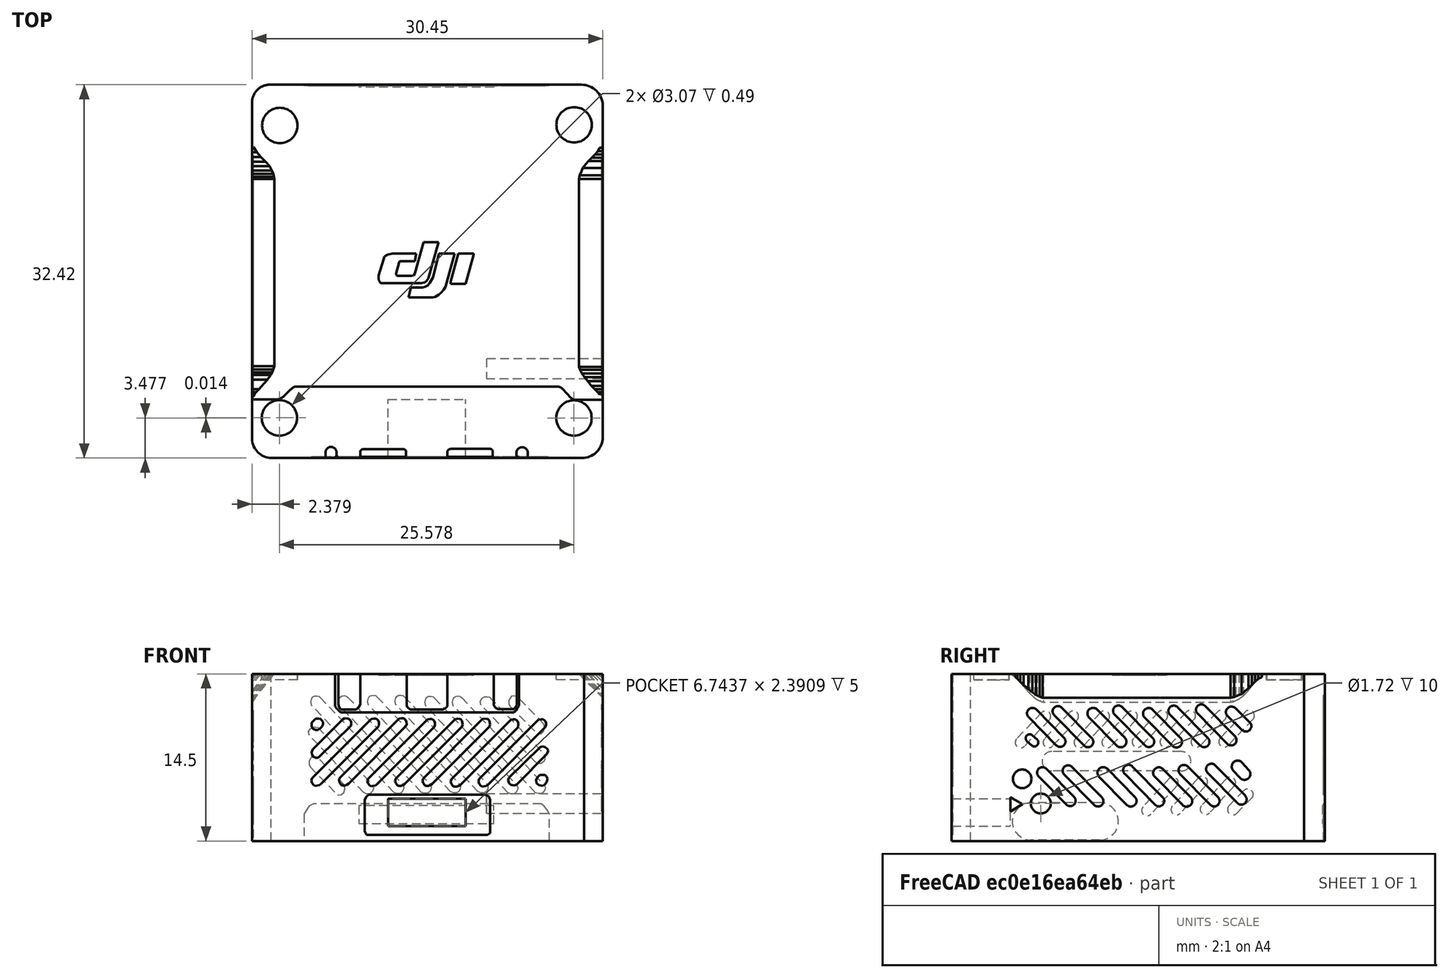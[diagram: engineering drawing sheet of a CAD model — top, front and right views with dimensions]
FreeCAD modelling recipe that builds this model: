
FCSTD DOCUMENT  (FreeCAD 0.19R24267 +99 (Git))
Label: O3
License: All rights reserved
LicenseURL: http://en.wikipedia.org/wiki/All_rights_reserved
objects: Sketcher::SketchObject×13, PartDesign::Pocket×10, Image::ImagePlane×5, PartDesign::Pad×1, PartDesign::Groove×1, PartDesign::SubtractivePipe×1, PartDesign::Body×1, Mesh::Feature×1
note: 40 computed .brp shape members not serialized (recipe doc carries the construction recipe); baked Part::Feature solids carry a one-line shape summary decoded from their .brp

FEATURE [Image::ImagePlane] ImagePlane
  XSize = 48.9538
  YSize = 52.2174
FEATURE [Sketcher::SketchObject] Sketch
  FullyConstrained = false
  MapMode = 5
  Support = -> [XY_Plane]
  sketch-geometry (8):
    g0: LineSegment StartX=-16.2841 StartY=17.4805 StartZ=0 EndX=10.6683 EndY=17.4805 EndZ=0
    g1: ArcOfCircle CenterX=10.6683 CenterY=15.6352 CenterZ=0 NormalX=0 NormalY=0 NormalZ=1 AngleXU=0 Radius=1.84529 StartAngle=0.0193587 EndAngle=1.5708
    g2: LineSegment StartX=12.5133 StartY=15.6709 StartZ=0 EndX=12.5133 EndY=-13.1285 EndZ=0
    g3: ArcOfCircle CenterX=10.6918 CenterY=-13.1285 CenterZ=0 NormalX=0 NormalY=0 NormalZ=1 AngleXU=0 Radius=1.82149 StartAngle=4.82467 EndAngle=6.28319
    g4: LineSegment StartX=10.8959 StartY=-14.9386 StartZ=0 EndX=-16.2285 EndY=-14.9386 EndZ=0
    g5: ArcOfCircle CenterX=-16.2285 CenterY=-13.2275 CenterZ=0 NormalX=0 NormalY=0 NormalZ=1 AngleXU=0 Radius=1.71109 StartAngle=3.16988 EndAngle=4.71239
    g6: LineSegment StartX=-17.9389 StartY=-13.2759 StartZ=0 EndX=-17.9389 EndY=15.9202 EndZ=0
    g7: ArcOfCircle CenterX=-16.3759 CenterY=15.9202 CenterZ=0 NormalX=0 NormalY=0 NormalZ=1 AngleXU=0 Radius=1.56302 StartAngle=1.51209 EndAngle=3.14159
  constraints (12):
    c: Horizontal(g0)
    c: Tangent(g0,g1) = 1.5708
    c: Coincident(g1,g2)
    c: Vertical(g2)
    c: Tangent(g2,g3) = 1.5708
    c: Coincident(g3,g4)
    c: Horizontal(g4)
    c: Tangent(g4,g5) = 1.5708
    c: Coincident(g5,g6)
    c: Vertical(g6)
    c: Tangent(g6,g7) = 1.5708
    c: Coincident(g7,g0)
FEATURE [PartDesign::Pad] Pad
  Direction = (1,1,1)
  Length = 14.5
  Length2 = 100
  Profile = -> Sketch
  Type = 0
FEATURE [Sketcher::SketchObject] Sketch001
  FullyConstrained = false
  MapMode = 5
  Placement = pos=(0,0,14.5) rot=(0,0,1;0rad)
  Support = -> [Pad]
  sketch-geometry (4):
    g0: Circle CenterX=-15.5269 CenterY=13.9364 CenterZ=0 NormalX=0 NormalY=0 NormalZ=1 AngleXU=0 Radius=1.53652
    g1: Circle CenterX=10.0286 CenterY=13.9974 CenterZ=0 NormalX=0 NormalY=0 NormalZ=1 AngleXU=0 Radius=1.53652
    g2: Circle CenterX=-15.561 CenterY=-11.4486 CenterZ=0 NormalX=0 NormalY=0 NormalZ=1 AngleXU=0 Radius=1.53652
    g3: Circle CenterX=10.0174 CenterY=-11.4626 CenterZ=0 NormalX=0 NormalY=0 NormalZ=1 AngleXU=0 Radius=1.53652
FEATURE [PartDesign::Pocket] Pocket
  BaseFeature = -> Pad
  Length = 0.5
  Length2 = 100
  Profile = -> Sketch001
  Type = 0
FEATURE [Sketcher::SketchObject] Sketch002
  FullyConstrained = false
  MapMode = 5
  Placement = pos=(0,0,14.5) rot=(0,0,1;0rad)
  Support = -> [Pocket]
  sketch-geometry (49):
    g0: LineSegment StartX=-3.66775 StartY=2.80694 StartZ=0 EndX=-5.73284 EndY=2.80694 EndZ=0
    g1: LineSegment StartX=-5.73284 StartY=2.80694 StartZ=0 EndX=-6.1577 EndY=2.70892 EndZ=0
    g2: LineSegment StartX=-6.1577 StartY=2.70892 StartZ=0 EndX=-6.42677 EndY=2.55314 EndZ=0
    g3: LineSegment StartX=-6.42677 StartY=2.55314 StartZ=0 EndX=-6.5157 EndY=2.35716 EndZ=0
    g4: LineSegment StartX=-6.5157 StartY=2.35716 StartZ=0 EndX=-6.9475 EndY=0.92689 EndZ=0
    g5: LineSegment StartX=-6.9475 StartY=0.92689 StartZ=0 EndX=-6.957 EndY=0.670578 EndZ=0
    g6: LineSegment StartX=-6.957 StartY=0.670578 StartZ=0 EndX=-6.92852 EndY=0.480717 EndZ=0
    g7: LineSegment StartX=-6.92852 StartY=0.480717 StartZ=0 EndX=-6.85411 EndY=0.359586 EndZ=0
    g8: LineSegment StartX=-6.85411 StartY=0.359586 StartZ=0 EndX=-6.79407 EndY=0.288105 EndZ=0
    g9: LineSegment StartX=-6.79407 StartY=0.288105 StartZ=0 EndX=-6.74546 EndY=0.256653 EndZ=0
    g10: LineSegment StartX=-6.74546 StartY=0.256653 StartZ=0 EndX=-3.2332 EndY=0.256653 EndZ=0
    g11: LineSegment StartX=-3.2332 StartY=0.256653 StartZ=0 EndX=-2.93381 EndY=0.321952 EndZ=0
    g12: LineSegment StartX=-2.93381 StartY=0.321952 StartZ=0 EndX=-2.79803 EndY=0.434318 EndZ=0
    g13: LineSegment StartX=-2.79803 StartY=0.434318 StartZ=0 EndX=-2.63651 EndY=0.663731 EndZ=0
    g14: LineSegment StartX=-2.63651 StartY=0.663731 StartZ=0 EndX=-1.72995 EndY=3.79902 EndZ=0
    g15: LineSegment StartX=-1.72995 StartY=3.79902 StartZ=0 EndX=-3.0436 EndY=3.79902 EndZ=0
    g16: LineSegment StartX=-3.0436 StartY=3.79902 StartZ=0 EndX=-3.79676 EndY=1.0627 EndZ=0
    g17: LineSegment StartX=-3.79676 StartY=1.0627 StartZ=0 EndX=-3.91067 EndY=0.929798 EndZ=0
    g18: LineSegment StartX=-3.91067 StartY=0.929798 StartZ=0 EndX=-4.08155 EndY=0.882333 EndZ=0
    g19: LineSegment StartX=-4.08155 StartY=0.882333 StartZ=0 EndX=-5.34413 EndY=0.882333 EndZ=0
    g20: LineSegment StartX=-5.34413 StartY=0.882333 StartZ=0 EndX=-5.42956 EndY=0.96777 EndZ=0
    g21: LineSegment StartX=-5.42956 StartY=0.96777 StartZ=0 EndX=-5.42956 EndY=1.11966 EndZ=0
    g22: LineSegment StartX=-5.42956 StartY=1.11966 StartZ=0 EndX=-5.18132 EndY=2.01186 EndZ=0
    g23: LineSegment StartX=-5.18132 StartY=2.01186 StartZ=0 EndX=-5.14987 EndY=2.11479 EndZ=0
    g24: LineSegment StartX=-5.14987 StartY=2.11479 StartZ=0 EndX=-5.10984 EndY=2.16054 EndZ=0
    g25: LineSegment StartX=-5.10984 StartY=2.16054 StartZ=0 EndX=-3.79458 EndY=2.16054 EndZ=0
    g26: LineSegment StartX=-3.79458 StartY=2.16054 StartZ=0 EndX=-3.66775 EndY=2.80694 EndZ=0
    g27: LineSegment StartX=-1.69511 StartY=2.81981 StartZ=0 EndX=-0.339263 EndY=2.81981 EndZ=0
    g28: LineSegment StartX=-0.339263 StartY=2.81981 StartZ=0 EndX=-1.14003 EndY=-0.062406 EndZ=0
    g29: LineSegment StartX=-1.14003 StartY=-0.062406 StartZ=0 EndX=-1.30548 EndY=-0.316942 EndZ=0
    g30: LineSegment StartX=-1.30548 StartY=-0.316942 StartZ=0 EndX=-1.5282 EndY=-0.584204 EndZ=0
    g31: LineSegment StartX=-1.5282 StartY=-0.584204 StartZ=0 EndX=-1.73182 EndY=-0.756015 EndZ=0
    g32: LineSegment StartX=-1.73182 StartY=-0.756015 StartZ=0 EndX=-2.05636 EndY=-0.95328 EndZ=0
    g33: LineSegment StartX=-2.05636 StartY=-0.95328 StartZ=0 EndX=-2.23453 EndY=-0.997824 EndZ=0
    g34: LineSegment StartX=-2.23453 StartY=-0.997824 StartZ=0 EndX=-4.3599 EndY=-0.997824 EndZ=0
    g35: LineSegment StartX=-4.3599 StartY=-0.997824 StartZ=0 EndX=-4.14991 EndY=-0.170584 EndZ=0
    g36: LineSegment StartX=-4.14991 StartY=-0.170584 StartZ=0 EndX=-4.10532 EndY=-0.133615 EndZ=0
    g37: LineSegment StartX=-4.10532 StartY=-0.133615 StartZ=0 EndX=-3.13796 EndY=-0.133615 EndZ=0
    g38: LineSegment StartX=-3.13796 StartY=-0.133615 StartZ=0 EndX=-2.92144 EndY=-0.077738 EndZ=0
    g39: LineSegment StartX=-2.92144 StartY=-0.077738 StartZ=0 EndX=-2.66999 EndY=0.065446 EndZ=0
    g40: LineSegment StartX=-2.66999 StartY=0.065446 StartZ=0 EndX=-2.48839 EndY=0.264507 EndZ=0
    g41: LineSegment StartX=-2.48839 StartY=0.264507 StartZ=0 EndX=-2.21691 EndY=0.751707 EndZ=0
    g42: LineSegment StartX=-2.21691 StartY=0.751707 StartZ=0 EndX=-1.69511 EndY=2.81981 EndZ=0
    g43: LineSegment StartX=-0.02724 StartY=2.80822 StartZ=0 EndX=1.30487 EndY=2.80822 EndZ=0
    g44: LineSegment StartX=1.30487 StartY=2.80822 StartZ=0 EndX=1.31884 EndY=2.72222 EndZ=0
    g45: LineSegment StartX=1.31884 StartY=2.72222 StartZ=0 EndX=0.594821 EndY=0.171477 EndZ=0
    g46: LineSegment StartX=0.594821 StartY=0.171477 StartZ=0 EndX=-0.701894 EndY=0.171477 EndZ=0
    g47: LineSegment StartX=-0.701894 StartY=0.171477 StartZ=0 EndX=-0.693363 EndY=0.363425 EndZ=0
    g48: LineSegment StartX=-0.693363 StartY=0.363425 StartZ=0 EndX=-0.02724 EndY=2.80822 EndZ=0
  constraints (60):
    c: Horizontal(g0)
    c: Coincident(g0,g1)
    c: Coincident(g1,g2)
    c: Coincident(g2,g3)
    c: Coincident(g3,g4)
    c: Coincident(g4,g5)
    c: Coincident(g5,g6)
    c: Coincident(g6,g7)
    c: Coincident(g7,g8)
    c: Coincident(g8,g9)
    c: Coincident(g9,g10)
    c: Horizontal(g10)
    c: Coincident(g10,g11)
    c: Coincident(g11,g12)
    c: Coincident(g12,g13)
    c: Coincident(g13,g14)
    c: Coincident(g14,g15)
    c: Horizontal(g15)
    c: Coincident(g15,g16)
    c: Coincident(g16,g17)
    c: Coincident(g17,g18)
    c: Coincident(g18,g19)
    c: Horizontal(g19)
    c: Coincident(g19,g20)
    c: Coincident(g20,g21)
    c: Vertical(g21)
    c: Coincident(g21,g22)
    c: Coincident(g22,g23)
    c: Coincident(g23,g24)
    c: Coincident(g24,g25)
    c: Horizontal(g25)
    c: Coincident(g25,g26)
    c: Coincident(g26,g0)
    c: Horizontal(g27)
    c: Coincident(g27,g28)
    c: Coincident(g28,g29)
    c: Coincident(g29,g30)
    c: Coincident(g30,g31)
    c: Coincident(g31,g32)
    c: Coincident(g32,g33)
    c: Coincident(g33,g34)
    c: Horizontal(g34)
    c: Coincident(g34,g35)
    c: Coincident(g35,g36)
    c: Coincident(g36,g37)
    c: Horizontal(g37)
    c: Coincident(g37,g38)
    c: Coincident(g38,g39)
    c: Coincident(g39,g40)
    c: Coincident(g40,g41)
    c: Coincident(g41,g42)
    c: Coincident(g42,g27)
    c: Horizontal(g43)
    c: Coincident(g43,g44)
    c: Coincident(g44,g45)
    c: Coincident(g45,g46)
    c: Horizontal(g46)
    c: Coincident(g46,g47)
    c: Coincident(g47,g48)
    c: Coincident(g48,g43)
FEATURE [PartDesign::Pocket] Pocket001
  BaseFeature = -> Pocket
  Length = 0.1
  Length2 = 100
  Profile = -> Sketch002
  Type = 0
FEATURE [Sketcher::SketchObject] Sketch003
  FullyConstrained = false
  MapMode = 5
  Placement = pos=(0,0,14.5) rot=(0,0,1;0rad)
  Support = -> [Pocket001]
  sketch-geometry (21):
    g0: LineSegment StartX=-17.8135 StartY=12.0585 StartZ=0 EndX=-17.5216 EndY=11.6173 EndZ=0
    g1: LineSegment StartX=-17.5216 StartY=11.6173 StartZ=0 EndX=-17.1624 EndY=11.1947 EndZ=0
    g2: LineSegment StartX=-17.1624 StartY=11.1947 StartZ=0 EndX=-16.761 EndY=10.7933 EndZ=0
    g3: LineSegment StartX=-16.761 StartY=10.7933 StartZ=0 EndX=-16.4229 EndY=10.3944 EndZ=0
    g4: LineSegment StartX=-16.4229 StartY=10.3944 StartZ=0 EndX=-16.2286 EndY=10.0369 EndZ=0
    g5: LineSegment StartX=-16.2286 StartY=10.0369 StartZ=0 EndX=-16.1042 EndY=9.73377 EndZ=0
    g6: LineSegment StartX=-16.1042 StartY=9.73377 StartZ=0 EndX=-16.0187 EndY=9.49283 EndZ=0
    g7: LineSegment StartX=-16.0187 StartY=9.49283 StartZ=0 EndX=-16.011 EndY=9.30629 EndZ=0
    g8: LineSegment StartX=-16.011 StartY=9.30629 StartZ=0 EndX=-16.011 EndY=-6.96555 EndZ=0
    g9: LineSegment StartX=-16.011 StartY=-6.96555 StartZ=0 EndX=-16.0855 EndY=-7.2519 EndZ=0
    g10: LineSegment StartX=-16.0855 StartY=-7.2519 StartZ=0 EndX=-16.1811 EndY=-7.51099 EndZ=0
    g11: LineSegment StartX=-16.1811 StartY=-7.51099 StartZ=0 EndX=-16.3084 EndY=-7.72734 EndZ=0
    g12: LineSegment StartX=-16.3084 StartY=-7.72734 StartZ=0 EndX=-16.6066 EndY=-8.14057 EndZ=0
    g13: LineSegment StartX=-16.6066 StartY=-8.14057 StartZ=0 EndX=-16.92 EndY=-8.48903 EndZ=0
    g14: LineSegment StartX=-16.92 StartY=-8.48903 StartZ=0 EndX=-17.3378 EndY=-8.9503 EndZ=0
    g15: LineSegment StartX=-17.3378 StartY=-8.9503 StartZ=0 EndX=-17.5885 EndY=-9.21663 EndZ=0
    g16: LineSegment StartX=-17.5885 StartY=-9.21663 StartZ=0 EndX=-17.7086 EndY=-9.38713 EndZ=0
    g17: LineSegment StartX=-17.7086 StartY=-9.38713 StartZ=0 EndX=-17.8088 EndY=-9.57859 EndZ=0
    g18: LineSegment StartX=-17.8088 StartY=-9.57859 StartZ=0 EndX=-18.1875 EndY=-9.6359 EndZ=0
    g19: LineSegment StartX=-18.1875 StartY=-9.6359 StartZ=0 EndX=-18.1875 EndY=12.0985 EndZ=0
    g20: LineSegment StartX=-18.1875 StartY=12.0985 StartZ=0 EndX=-17.8135 EndY=12.0585 EndZ=0
  constraints (23):
    c: Coincident(g0,g1)
    c: Coincident(g1,g2)
    c: Coincident(g2,g3)
    c: Coincident(g3,g4)
    c: Coincident(g4,g5)
    c: Coincident(g5,g6)
    c: Coincident(g6,g7)
    c: Coincident(g7,g8)
    c: Vertical(g8)
    c: Coincident(g8,g9)
    c: Coincident(g9,g10)
    c: Coincident(g10,g11)
    c: Coincident(g11,g12)
    c: Coincident(g12,g13)
    c: Coincident(g13,g14)
    c: Coincident(g14,g15)
    c: Coincident(g15,g16)
    c: Coincident(g16,g17)
    c: Coincident(g17,g18)
    c: Coincident(g18,g19)
    c: Vertical(g19)
    c: Coincident(g19,g20)
    c: Coincident(g20,g0)
FEATURE [PartDesign::Groove] Groove
  Angle = 360
  Axis = (1e-16,1,-1e-16)
  Base = (0,0,0)
  BaseFeature = -> Pocket001
  Profile = -> Sketch003
  ReferenceAxis = -> Y_Axis
  Reversed = true
FEATURE [Sketcher::SketchObject] Sketch004
  FullyConstrained = false
  MapMode = 5
  Placement = pos=(0,0,14.5) rot=(0,0,1;0rad)
  Support = -> [Groove]
  sketch-geometry (21):
    g0: LineSegment StartX=12.785 StartY=12.1444 StartZ=0 EndX=12.2358 EndY=12.0001 EndZ=0
    g1: LineSegment StartX=12.2358 StartY=12.0001 StartZ=0 EndX=12.0941 EndY=11.7027 EndZ=0
    g2: LineSegment StartX=12.0941 StartY=11.7027 StartZ=0 EndX=11.8534 EndY=11.4336 EndZ=0
    g3: LineSegment StartX=11.8534 StartY=11.4336 StartZ=0 EndX=11.5701 EndY=11.1504 EndZ=0
    g4: LineSegment StartX=11.5701 StartY=11.1504 StartZ=0 EndX=11.2727 EndY=10.8672 EndZ=0
    g5: LineSegment StartX=11.2727 StartY=10.8672 StartZ=0 EndX=11.0461 EndY=10.5839 EndZ=0
    g6: LineSegment StartX=11.0461 StartY=10.5839 StartZ=0 EndX=10.7771 EndY=10.244 EndZ=0
    g7: LineSegment StartX=10.7771 StartY=10.244 StartZ=0 EndX=10.6638 EndY=9.97494 EndZ=0
    g8: LineSegment StartX=10.6638 StartY=9.97494 StartZ=0 EndX=10.508 EndY=9.60673 EndZ=0
    g9: LineSegment StartX=10.508 StartY=9.60673 StartZ=0 EndX=10.4372 EndY=9.30932 EndZ=0
    g10: LineSegment StartX=10.4372 StartY=9.30932 StartZ=0 EndX=10.4372 EndY=-7.02887 EndZ=0
    g11: LineSegment StartX=10.4372 StartY=-7.02887 StartZ=0 EndX=10.5543 EndY=-7.27237 EndZ=0
    g12: LineSegment StartX=10.5543 StartY=-7.27237 StartZ=0 EndX=10.6934 EndY=-7.58543 EndZ=0
    g13: LineSegment StartX=10.6934 StartY=-7.58543 StartZ=0 EndX=10.9142 EndY=-7.90996 EndZ=0
    g14: LineSegment StartX=10.9142 StartY=-7.90996 StartZ=0 EndX=11.2069 EndY=-8.25359 EndZ=0
    g15: LineSegment StartX=11.2069 StartY=-8.25359 StartZ=0 EndX=11.5441 EndY=-8.67357 EndZ=0
    g16: LineSegment StartX=11.5441 StartY=-8.67357 StartZ=0 EndX=11.8305 EndY=-8.9472 EndZ=0
    g17: LineSegment StartX=11.8305 StartY=-8.9472 StartZ=0 EndX=12.085 EndY=-9.2272 EndZ=0
    g18: LineSegment StartX=12.085 StartY=-9.2272 StartZ=0 EndX=12.2123 EndY=-9.37992 EndZ=0
    g19: LineSegment StartX=12.2123 StartY=-9.37992 StartZ=0 EndX=12.785 EndY=-9.47537 EndZ=0
    g20: LineSegment StartX=12.785 StartY=-9.47537 StartZ=0 EndX=12.785 EndY=12.1444 EndZ=0
  constraints (23):
    c: Coincident(g0,g1)
    c: Coincident(g1,g2)
    c: Coincident(g2,g3)
    c: Coincident(g3,g4)
    c: Coincident(g4,g5)
    c: Coincident(g5,g6)
    c: Coincident(g6,g7)
    c: Coincident(g7,g8)
    c: Coincident(g8,g9)
    c: Coincident(g9,g10)
    c: Vertical(g10)
    c: Coincident(g10,g11)
    c: Coincident(g11,g12)
    c: Coincident(g12,g13)
    c: Coincident(g13,g14)
    c: Coincident(g14,g15)
    c: Coincident(g15,g16)
    c: Coincident(g16,g17)
    c: Coincident(g17,g18)
    c: Coincident(g18,g19)
    c: Coincident(g19,g20)
    c: Coincident(g20,g0)
    c: Vertical(g20)
FEATURE [Sketcher::SketchObject] Sketch005
  FullyConstrained = false
  MapMode = 5
  Placement = pos=(0,17.4805,0) rot=(0,0.707107,0.707107;3.14159rad)
  Support = -> [Groove]
  sketch-geometry (1):
    g0: LineSegment StartX=-12.754 StartY=14.4579 StartZ=0 EndX=-15.6892 EndY=11.5227 EndZ=0
  constraints (1):
    c: Angle(g0,g-2) = 0.785398
FEATURE [PartDesign::SubtractivePipe] SubtractivePipe
  AuxilleryCurvelinear = true
  AuxillerySpineTangent = false
  BaseFeature = -> Groove
  Binormal = (0,0,0)
  Mode = 0
  Profile = -> Sketch004
  Spine = -> Sketch005 [Edge1]
  SpineTangent = false
  Transformation = 0
  Transition = 0
FEATURE [Sketcher::SketchObject] Sketch006
  FullyConstrained = false
  MapMode = 5
  Placement = pos=(0,0,14.5) rot=(0,0,1;0rad)
  Support = -> [SubtractivePipe]
  sketch-geometry (32):
    g0: LineSegment StartX=-18.7368 StartY=-9.85693 StartZ=0 EndX=-15.9402 EndY=-9.85693 EndZ=0
    g1: ArcOfCircle CenterX=-15.9402 CenterY=-8.6812 CenterZ=0 NormalX=0 NormalY=0 NormalZ=1 AngleXU=0 Radius=1.17573 StartAngle=4.71239 EndAngle=5.49915
    g2: LineSegment StartX=-15.1077 StartY=-9.51143 StartZ=0 EndX=-14.7496 EndY=-9.15233 EndZ=0
    g3: ArcOfCircle CenterX=-12.453 CenterY=-11.4427 CenterZ=0 NormalX=0 NormalY=0 NormalZ=1 AngleXU=0 Radius=3.2435 StartAngle=2.14933 EndAngle=2.35756
    g4: LineSegment StartX=-14.2265 StartY=-8.72703 StartZ=0 EndX=8.55128 EndY=-8.72703 EndZ=0
    g5: ArcOfCircle CenterX=8.55128 CenterY=-9.36613 CenterZ=0 NormalX=0 NormalY=0 NormalZ=1 AngleXU=0 Radius=0.639103 StartAngle=0.772938 EndAngle=1.5708
    g6: LineSegment StartX=9.00879 StartY=-8.91988 StartZ=0 EndX=9.76154 EndY=-9.7069 EndZ=0
    g7: ArcOfCircle CenterX=10.1395 CenterY=-9.34542 CenterZ=0 NormalX=0 NormalY=0 NormalZ=1 AngleXU=0 Radius=0.522979 StartAngle=3.90474 EndAngle=4.75966
    g8: LineSegment StartX=10.1642 StartY=-9.86781 StartZ=0 EndX=12.9927 EndY=-9.86781 EndZ=0
    g9: LineSegment StartX=12.9927 StartY=-9.86781 StartZ=0 EndX=14.3964 EndY=-16.0549 EndZ=0
    g10: LineSegment StartX=14.3964 StartY=-16.0549 StartZ=0 EndX=6.0094 EndY=-15.3953 EndZ=0
    g11: LineSegment StartX=6.0094 StartY=-15.3953 StartZ=0 EndX=6.0094 EndY=-14.4746 EndZ=0
    g12: ArcOfCircle CenterX=5.51501 CenterY=-14.4884 CenterZ=0 NormalX=0 NormalY=0 NormalZ=1 AngleXU=0 Radius=0.49459 StartAngle=0.0279138 EndAngle=3.11701
    g13: LineSegment StartX=5.02057 StartY=-14.4763 StartZ=0 EndX=5.02299 EndY=-15.641 EndZ=0
    g14: LineSegment StartX=5.02299 StartY=-15.641 StartZ=0 EndX=2.96705 EndY=-15.641 EndZ=0
    g15: LineSegment StartX=2.96705 StartY=-15.641 StartZ=0 EndX=2.96705 EndY=-14.3888 EndZ=0
    g16: ArcOfCircle CenterX=2.72374 CenterY=-14.3888 CenterZ=0 NormalX=0 NormalY=0 NormalZ=1 AngleXU=0 Radius=0.243307 StartAngle=0 EndAngle=1.57581
    g17: LineSegment StartX=2.72252 StartY=-14.1455 StartZ=0 EndX=-0.676868 EndY=-14.1455 EndZ=0
    g18: ArcOfCircle CenterX=-0.676868 CenterY=-14.4517 CenterZ=0 NormalX=0 NormalY=0 NormalZ=1 AngleXU=0 Radius=0.3062 StartAngle=1.5708 EndAngle=3.07143
    g19: LineSegment StartX=-0.982315 StartY=-14.4303 StartZ=0 EndX=-0.982315 EndY=-15.3173 EndZ=0
    g20: LineSegment StartX=-0.982315 StartY=-15.3173 StartZ=0 EndX=-4.57718 EndY=-15.3173 EndZ=0
    g21: LineSegment StartX=-4.57718 StartY=-15.3173 StartZ=0 EndX=-4.56112 EndY=-14.3883 EndZ=0
    g22: ArcOfCircle CenterX=-4.7646 CenterY=-14.384 CenterZ=0 NormalX=0 NormalY=0 NormalZ=1 AngleXU=0 Radius=0.203524 StartAngle=6.26196 EndAngle=7.96565
    g23: LineSegment StartX=-4.78728 StartY=-14.1817 StartZ=0 EndX=-8.31122 EndY=-14.1817 EndZ=0
    g24: ArcOfCircle CenterX=-8.31122 CenterY=-14.4208 CenterZ=0 NormalX=0 NormalY=0 NormalZ=1 AngleXU=0 Radius=0.239068 StartAngle=1.5708 EndAngle=3.24723
    g25: LineSegment StartX=-8.54895 StartY=-14.446 StartZ=0 EndX=-8.54895 EndY=-15.2819 EndZ=0
    g26: LineSegment StartX=-8.54895 StartY=-15.2819 StartZ=0 EndX=-10.5986 EndY=-15.2819 EndZ=0
    g27: LineSegment StartX=-10.5986 StartY=-15.2819 StartZ=0 EndX=-10.5986 EndY=-14.4514 EndZ=0
    g28: ArcOfCircle CenterX=-11.0788 CenterY=-14.4514 CenterZ=0 NormalX=0 NormalY=0 NormalZ=1 AngleXU=0 Radius=0.480113 StartAngle=0 EndAngle=3.09716
    g29: LineSegment StartX=-11.5584 StartY=-14.43 StartZ=0 EndX=-11.5584 EndY=-15.3343 EndZ=0
    g30: LineSegment StartX=-11.5584 StartY=-15.3343 StartZ=0 EndX=-19.8266 EndY=-15.3343 EndZ=0
    g31: LineSegment StartX=-19.8266 StartY=-15.3343 StartZ=0 EndX=-18.7368 EndY=-9.85693 EndZ=0
  constraints (47):
    c: Horizontal(g0)
    c: Tangent(g0,g1) = -1.5708
    c: Tangent(g1,g2) = -1.5708
    c: Tangent(g2,g3) = 1.5708
    c: Coincident(g3,g4)
    c: Horizontal(g4)
    c: Tangent(g4,g5) = 1.5708
    c: Coincident(g5,g6)
    c: Tangent(g6,g7) = -1.5708
    c: Coincident(g7,g8)
    c: Horizontal(g8)
    c: Coincident(g8,g9)
    c: Coincident(g9,g10)
    c: Coincident(g10,g11)
    c: Vertical(g11)
    c: Coincident(g13,g14)
    c: Horizontal(g14)
    c: Coincident(g14,g15)
    c: Vertical(g15)
    c: Tangent(g15,g16) = -1.5708
    c: Coincident(g16,g17)
    c: Horizontal(g17)
    c: Tangent(g17,g18) = -1.5708
    c: Coincident(g18,g19)
    c: Vertical(g19)
    c: Coincident(g19,g20)
    c: Horizontal(g20)
    c: Coincident(g22,g23)
    c: Horizontal(g23)
    c: Tangent(g23,g24) = -1.5708
    c: Coincident(g24,g25)
    c: Vertical(g25)
    c: Coincident(g25,g26)
    c: Horizontal(g26)
    c: Coincident(g26,g27)
    c: Vertical(g27)
    c: Tangent(g27,g28) = -1.5708
    c: Coincident(g28,g29)
    c: Vertical(g29)
    c: Coincident(g29,g30)
    c: Horizontal(g30)
    c: Coincident(g30,g31)
    c: Coincident(g31,g0)
    c: Coincident(g11,g12)
    c: Coincident(g13,g12)
    c: Coincident(g22,g21)
    c: Coincident(g20,g21)
FEATURE [PartDesign::Pocket] Pocket002
  BaseFeature = -> SubtractivePipe
  Length = 0.01
  Length2 = 100
  Profile = -> Sketch006
  Type = 0
FEATURE [Image::ImagePlane] ImagePlane001
  Placement = pos=(-0.6,-14,4.6) rot=(-1,0,0;4.71239rad)
  XSize = 43.6829
  YSize = 28.6523
FEATURE [Sketcher::SketchObject] Sketch007
  FullyConstrained = false
  MapMode = 5
  Placement = pos=(0,-14.9386,0) rot=(1,0,0;1.5708rad)
  Support = -> [Pocket002]
  sketch-geometry (212):
    g0: LineSegment StartX=-12.4029 StartY=10.6388 StartZ=0 EndX=-12.7611 EndY=10.2806 EndZ=0
    g1: LineSegment StartX=-12.7611 StartY=10.2806 StartZ=0 EndX=-12.7611 EndY=9.9015 EndZ=0
    g2: LineSegment StartX=-12.7611 StartY=9.9015 StartZ=0 EndX=-12.6292 EndY=9.7423 EndZ=0
    g3: LineSegment StartX=-12.6292 StartY=9.7423 StartZ=0 EndX=-12.4029 EndY=9.64176 EndZ=0
    g4: LineSegment StartX=-12.4029 StartY=9.64176 StartZ=0 EndX=-12.2186 EndY=9.65014 EndZ=0
    g5: LineSegment StartX=-12.2186 StartY=9.65014 StartZ=0 EndX=-11.984 EndY=9.7842 EndZ=0
    g6: LineSegment StartX=-11.984 StartY=9.7842 StartZ=0 EndX=-11.8667 EndY=9.91826 EndZ=0
    g7: LineSegment StartX=-11.8667 StartY=9.91826 StartZ=0 EndX=-11.7745 EndY=10.1277 EndZ=0
    g8: LineSegment StartX=-11.7745 StartY=10.1277 StartZ=0 EndX=-11.7745 EndY=10.354 EndZ=0
    g9: LineSegment StartX=-11.7745 StartY=10.354 StartZ=0 EndX=-11.8918 EndY=10.488 EndZ=0
    g10: LineSegment StartX=-11.8918 StartY=10.488 StartZ=0 EndX=-12.0008 EndY=10.5969 EndZ=0
    g11: LineSegment StartX=-12.0008 StartY=10.5969 StartZ=0 EndX=-12.1683 EndY=10.6305 EndZ=0
    g12: LineSegment StartX=-12.1683 StartY=10.6305 StartZ=0 EndX=-12.4029 EndY=10.6388 EndZ=0
    g13: LineSegment StartX=-9.88903 StartY=10.646 StartZ=0 EndX=-10.0598 EndY=10.5452 EndZ=0
    g14: LineSegment StartX=-10.0598 StartY=10.5452 StartZ=0 EndX=-12.6695 EndY=7.94572 EndZ=0
    g15: LineSegment StartX=-12.6695 StartY=7.94572 StartZ=0 EndX=-12.7507 EndY=7.68779 EndZ=0
    g16: LineSegment StartX=-12.7507 StartY=7.68779 StartZ=0 EndX=-12.737 EndY=7.47513 EndZ=0
    g17: LineSegment StartX=-12.737 StartY=7.47513 StartZ=0 EndX=-12.6341 EndY=7.33107 EndZ=0
    g18: LineSegment StartX=-12.6341 StartY=7.33107 StartZ=0 EndX=-12.4145 EndY=7.23503 EndZ=0
    g19: LineSegment StartX=-12.4145 StartY=7.23503 StartZ=0 EndX=-12.2568 EndY=7.23503 EndZ=0
    g20: LineSegment StartX=-12.2568 StartY=7.23503 StartZ=0 EndX=-12.1127 EndY=7.29677 EndZ=0
    g21: LineSegment StartX=-12.1127 StartY=7.29677 StartZ=0 EndX=-9.35496 EndY=9.97905 EndZ=0
    g22: LineSegment StartX=-9.35496 StartY=9.97905 StartZ=0 EndX=-9.32066 EndY=10.1505 EndZ=0
    g23: LineSegment StartX=-9.32066 StartY=10.1505 StartZ=0 EndX=-9.33262 EndY=10.3471 EndZ=0
    g24: LineSegment StartX=-9.33262 StartY=10.3471 StartZ=0 EndX=-9.3924 EndY=10.4575 EndZ=0
    g25: LineSegment StartX=-9.3924 StartY=10.4575 StartZ=0 EndX=-9.46597 EndY=10.5219 EndZ=0
    g26: LineSegment StartX=-9.46597 StartY=10.5219 StartZ=0 EndX=-9.55794 EndY=10.6092 EndZ=0
    g27: LineSegment StartX=-9.55794 StartY=10.6092 StartZ=0 EndX=-9.65911 EndY=10.6276 EndZ=0
    g28: LineSegment StartX=-9.65911 StartY=10.6276 StartZ=0 EndX=-9.88903 EndY=10.646 EndZ=0
    g29: LineSegment StartX=-7.56818 StartY=10.598 StartZ=0 EndX=-12.7348 EndY=5.43639 EndZ=0
    g30: LineSegment StartX=-12.7348 StartY=5.43639 StartZ=0 EndX=-12.785 EndY=5.22691 EndZ=0
    g31: LineSegment StartX=-12.785 StartY=5.22691 StartZ=0 EndX=-12.7348 EndY=5.05096 EndZ=0
    g32: LineSegment StartX=-12.7348 StartY=5.05096 StartZ=0 EndX=-12.6091 EndY=4.875 EndZ=0
    g33: LineSegment StartX=-12.6091 StartY=4.875 StartZ=0 EndX=-12.475 EndY=4.79121 EndZ=0
    g34: LineSegment StartX=-12.475 StartY=4.79121 StartZ=0 EndX=-12.2823 EndY=4.80797 EndZ=0
    g35: LineSegment StartX=-12.2823 StartY=4.80797 StartZ=0 EndX=-12.1063 EndY=4.85824 EndZ=0
    g36: LineSegment StartX=-12.1063 StartY=4.85824 StartZ=0 EndX=-11.9555 EndY=4.95041 EndZ=0
    g37: LineSegment StartX=-11.9555 StartY=4.95041 StartZ=0 EndX=-6.96159 EndY=9.95775 EndZ=0
    g38: LineSegment StartX=-6.96159 StartY=9.95775 StartZ=0 EndX=-6.91104 EndY=10.1375 EndZ=0
    g39: LineSegment StartX=-6.91104 StartY=10.1375 StartZ=0 EndX=-6.92789 EndY=10.3116 EndZ=0
    g40: LineSegment StartX=-6.92789 StartY=10.3116 StartZ=0 EndX=-6.98967 EndY=10.4689 EndZ=0
    g41: LineSegment StartX=-6.98967 StartY=10.4689 StartZ=0 EndX=-7.08515 EndY=10.5756 EndZ=0
    g42: LineSegment StartX=-7.08515 StartY=10.5756 StartZ=0 EndX=-7.16378 EndY=10.6261 EndZ=0
    g43: LineSegment StartX=-7.16378 StartY=10.6261 StartZ=0 EndX=-7.36598 EndY=10.6373 EndZ=0
    g44: LineSegment StartX=-7.36598 StartY=10.6373 StartZ=0 EndX=-7.56818 EndY=10.598 EndZ=0
    g45: LineSegment StartX=-4.5588 StartY=9.9759 StartZ=0 EndX=-4.50826 EndY=10.1556 EndZ=0
    g46: LineSegment StartX=-4.50826 StartY=10.1556 StartZ=0 EndX=-4.5251 EndY=10.3297 EndZ=0
    g47: LineSegment StartX=-4.5251 StartY=10.3297 StartZ=0 EndX=-4.58689 EndY=10.487 EndZ=0
    g48: LineSegment StartX=-4.58689 StartY=10.487 StartZ=0 EndX=-4.68237 EndY=10.5937 EndZ=0
    g49: LineSegment StartX=-4.68237 StartY=10.5937 StartZ=0 EndX=-4.761 EndY=10.6443 EndZ=0
    g50: LineSegment StartX=-4.761 StartY=10.6443 StartZ=0 EndX=-4.96319 EndY=10.6555 EndZ=0
    g51: LineSegment StartX=-4.96319 StartY=10.6555 StartZ=0 EndX=-5.16539 EndY=10.6162 EndZ=0
    g52: LineSegment StartX=-10.332 StartY=5.45454 StartZ=0 EndX=-10.3823 EndY=5.24507 EndZ=0
    g53: LineSegment StartX=-10.3823 StartY=5.24507 StartZ=0 EndX=-10.332 EndY=5.06911 EndZ=0
    g54: LineSegment StartX=-10.332 StartY=5.06911 StartZ=0 EndX=-10.2063 EndY=4.89316 EndZ=0
    g55: LineSegment StartX=-10.2063 StartY=4.89316 StartZ=0 EndX=-10.0722 EndY=4.80937 EndZ=0
    g56: LineSegment StartX=-10.0722 StartY=4.80937 StartZ=0 EndX=-9.87952 EndY=4.82613 EndZ=0
    g57: LineSegment StartX=-9.87952 StartY=4.82613 StartZ=0 EndX=-9.70356 EndY=4.8764 EndZ=0
    g58: LineSegment StartX=-9.70356 StartY=4.8764 StartZ=0 EndX=-9.55274 EndY=4.96857 EndZ=0
    g59: LineSegment StartX=-9.55274 StartY=4.96857 StartZ=0 EndX=-4.5588 EndY=9.9759 EndZ=0
    g60: LineSegment StartX=-5.16539 StartY=10.6162 StartZ=0 EndX=-10.332 EndY=5.45454 EndZ=0
    g61: LineSegment StartX=-2.09958 StartY=9.91598 StartZ=0 EndX=-2.04903 EndY=10.0957 EndZ=0
    g62: LineSegment StartX=-2.04903 StartY=10.0957 StartZ=0 EndX=-2.06588 EndY=10.2698 EndZ=0
    g63: LineSegment StartX=-2.06588 StartY=10.2698 StartZ=0 EndX=-2.12766 EndY=10.4271 EndZ=0
    g64: LineSegment StartX=-2.12766 StartY=10.4271 StartZ=0 EndX=-2.22315 EndY=10.5338 EndZ=0
    g65: LineSegment StartX=-2.22315 StartY=10.5338 StartZ=0 EndX=-2.30178 EndY=10.5844 EndZ=0
    g66: LineSegment StartX=-2.30178 StartY=10.5844 StartZ=0 EndX=-2.50397 EndY=10.5956 EndZ=0
    g67: LineSegment StartX=-2.50397 StartY=10.5956 StartZ=0 EndX=-2.70617 EndY=10.5563 EndZ=0
    g68: LineSegment StartX=0.303204 StartY=9.93414 StartZ=0 EndX=0.353753 EndY=10.1139 EndZ=0
    g69: LineSegment StartX=0.353753 StartY=10.1139 StartZ=0 EndX=0.336903 EndY=10.288 EndZ=0
    g70: LineSegment StartX=0.336903 StartY=10.288 StartZ=0 EndX=0.275121 EndY=10.4452 EndZ=0
    g71: LineSegment StartX=0.275121 StartY=10.4452 StartZ=0 EndX=0.17964 EndY=10.552 EndZ=0
    g72: LineSegment StartX=0.17964 StartY=10.552 StartZ=0 EndX=0.101009 EndY=10.6025 EndZ=0
    g73: LineSegment StartX=0.101009 StartY=10.6025 StartZ=0 EndX=-0.101187 EndY=10.6137 EndZ=0
    g74: LineSegment StartX=-0.101187 StartY=10.6137 StartZ=0 EndX=-0.303382 EndY=10.5744 EndZ=0
    g75: LineSegment StartX=-2.70617 StartY=10.5563 StartZ=0 EndX=-7.87275 EndY=5.39462 EndZ=0
    g76: LineSegment StartX=-7.87275 StartY=5.39462 StartZ=0 EndX=-7.92303 EndY=5.18515 EndZ=0
    g77: LineSegment StartX=-7.92303 StartY=5.18515 StartZ=0 EndX=-7.87275 EndY=5.00919 EndZ=0
    g78: LineSegment StartX=-7.87275 StartY=5.00919 StartZ=0 EndX=-7.74707 EndY=4.83324 EndZ=0
    g79: LineSegment StartX=-7.74707 StartY=4.83324 StartZ=0 EndX=-7.61301 EndY=4.74945 EndZ=0
    g80: LineSegment StartX=-7.61301 StartY=4.74945 StartZ=0 EndX=-7.4203 EndY=4.76621 EndZ=0
    g81: LineSegment StartX=-7.4203 StartY=4.76621 StartZ=0 EndX=-7.24434 EndY=4.81648 EndZ=0
    g82: LineSegment StartX=-7.24434 StartY=4.81648 StartZ=0 EndX=-7.09352 EndY=4.90865 EndZ=0
    g83: LineSegment StartX=-7.09352 StartY=4.90865 StartZ=0 EndX=-2.09958 EndY=9.91598 EndZ=0
    g84: LineSegment StartX=-5.46997 StartY=5.41278 StartZ=0 EndX=-5.52024 EndY=5.20331 EndZ=0
    g85: LineSegment StartX=-5.52024 StartY=5.20331 StartZ=0 EndX=-5.46997 EndY=5.02735 EndZ=0
    g86: LineSegment StartX=-5.46997 StartY=5.02735 StartZ=0 EndX=-5.34429 EndY=4.85139 EndZ=0
    g87: LineSegment StartX=-5.34429 StartY=4.85139 StartZ=0 EndX=-5.21023 EndY=4.7676 EndZ=0
    g88: LineSegment StartX=-5.21023 StartY=4.7676 StartZ=0 EndX=-5.01751 EndY=4.78436 EndZ=0
    g89: LineSegment StartX=-5.01751 StartY=4.78436 StartZ=0 EndX=-4.84155 EndY=4.83463 EndZ=0
    g90: LineSegment StartX=-4.84155 StartY=4.83463 StartZ=0 EndX=-4.69073 EndY=4.9268 EndZ=0
    g91: LineSegment StartX=-4.69073 StartY=4.9268 StartZ=0 EndX=0.303204 EndY=9.93414 EndZ=0
    g92: LineSegment StartX=-0.303382 StartY=10.5744 StartZ=0 EndX=-5.46997 EndY=5.41278 EndZ=0
    g93: LineSegment StartX=2.68454 StartY=9.93676 StartZ=0 EndX=2.73509 EndY=10.1165 EndZ=0
    g94: LineSegment StartX=2.73509 StartY=10.1165 StartZ=0 EndX=2.71824 EndY=10.2906 EndZ=0
    g95: LineSegment StartX=2.71824 StartY=10.2906 StartZ=0 EndX=2.65646 EndY=10.4479 EndZ=0
    g96: LineSegment StartX=2.65646 StartY=10.4479 StartZ=0 EndX=2.56098 EndY=10.5546 EndZ=0
    g97: LineSegment StartX=2.56098 StartY=10.5546 StartZ=0 EndX=2.48235 EndY=10.6051 EndZ=0
    g98: LineSegment StartX=2.48235 StartY=10.6051 StartZ=0 EndX=2.28015 EndY=10.6164 EndZ=0
    g99: LineSegment StartX=2.28015 StartY=10.6164 StartZ=0 EndX=2.07796 EndY=10.577 EndZ=0
    g100: LineSegment StartX=5.14377 StartY=9.87685 StartZ=0 EndX=5.19432 EndY=10.0566 EndZ=0
    g101: LineSegment StartX=5.19432 StartY=10.0566 StartZ=0 EndX=5.17747 EndY=10.2307 EndZ=0
    g102: LineSegment StartX=5.17747 StartY=10.2307 StartZ=0 EndX=5.11568 EndY=10.388 EndZ=0
    g103: LineSegment StartX=5.11568 StartY=10.388 StartZ=0 EndX=5.0202 EndY=10.4947 EndZ=0
    g104: LineSegment StartX=5.0202 StartY=10.4947 StartZ=0 EndX=4.94157 EndY=10.5452 EndZ=0
    g105: LineSegment StartX=4.94157 StartY=10.5452 StartZ=0 EndX=4.73938 EndY=10.5564 EndZ=0
    g106: LineSegment StartX=4.73938 StartY=10.5564 StartZ=0 EndX=4.53718 EndY=10.5171 EndZ=0
    g107: LineSegment StartX=7.54655 StartY=9.895 StartZ=0 EndX=7.5971 EndY=10.0747 EndZ=0
    g108: LineSegment StartX=7.5971 StartY=10.0747 StartZ=0 EndX=7.58025 EndY=10.2488 EndZ=0
    g109: LineSegment StartX=7.58025 StartY=10.2488 StartZ=0 EndX=7.51847 EndY=10.4061 EndZ=0
    g110: LineSegment StartX=7.51847 StartY=10.4061 StartZ=0 EndX=7.42299 EndY=10.5128 EndZ=0
    g111: LineSegment StartX=7.42299 StartY=10.5128 StartZ=0 EndX=7.34436 EndY=10.5634 EndZ=0
    g112: LineSegment StartX=7.34436 StartY=10.5634 StartZ=0 EndX=7.14216 EndY=10.5746 EndZ=0
    g113: LineSegment StartX=7.14216 StartY=10.5746 StartZ=0 EndX=6.93997 EndY=10.5353 EndZ=0
    g114: LineSegment StartX=-3.08863 StartY=5.4154 StartZ=0 EndX=-3.1389 EndY=5.20593 EndZ=0
    g115: LineSegment StartX=-3.1389 StartY=5.20593 StartZ=0 EndX=-3.08863 EndY=5.02997 EndZ=0
    g116: LineSegment StartX=-3.08863 StartY=5.02997 StartZ=0 EndX=-2.96295 EndY=4.85402 EndZ=0
    g117: LineSegment StartX=-2.96295 StartY=4.85402 StartZ=0 EndX=-2.82889 EndY=4.77023 EndZ=0
    g118: LineSegment StartX=-2.82889 StartY=4.77023 StartZ=0 EndX=-2.63617 EndY=4.78699 EndZ=0
    g119: LineSegment StartX=-2.63617 StartY=4.78699 StartZ=0 EndX=-2.46021 EndY=4.83726 EndZ=0
    g120: LineSegment StartX=-2.46021 StartY=4.83726 StartZ=0 EndX=-2.30939 EndY=4.92943 EndZ=0
    g121: LineSegment StartX=-2.30939 StartY=4.92943 StartZ=0 EndX=2.68454 EndY=9.93676 EndZ=0
    g122: LineSegment StartX=2.07796 StartY=10.577 StartZ=0 EndX=-3.08863 EndY=5.4154 EndZ=0
    g123: LineSegment StartX=4.53718 StartY=10.5171 StartZ=0 EndX=-0.629407 EndY=5.35548 EndZ=0
    g124: LineSegment StartX=-0.629407 StartY=5.35548 StartZ=0 EndX=-0.679681 EndY=5.14601 EndZ=0
    g125: LineSegment StartX=-0.679681 StartY=5.14601 StartZ=0 EndX=-0.629407 EndY=4.97006 EndZ=0
    g126: LineSegment StartX=-0.629407 StartY=4.97006 StartZ=0 EndX=-0.503724 EndY=4.7941 EndZ=0
    g127: LineSegment StartX=-0.503724 StartY=4.7941 StartZ=0 EndX=-0.369663 EndY=4.71031 EndZ=0
    g128: LineSegment StartX=-0.369663 StartY=4.71031 StartZ=0 EndX=-0.176948 EndY=4.72707 EndZ=0
    g129: LineSegment StartX=-0.176948 StartY=4.72707 StartZ=0 EndX=-0.000991 EndY=4.77734 EndZ=0
    g130: LineSegment StartX=-0.000991 StartY=4.77734 StartZ=0 EndX=0.149829 EndY=4.86951 EndZ=0
    g131: LineSegment StartX=0.149829 StartY=4.86951 StartZ=0 EndX=5.14377 EndY=9.87685 EndZ=0
    g132: LineSegment StartX=1.77338 StartY=5.37364 StartZ=0 EndX=1.72311 EndY=5.16417 EndZ=0
    g133: LineSegment StartX=1.72311 StartY=5.16417 StartZ=0 EndX=1.77338 EndY=4.98821 EndZ=0
    g134: LineSegment StartX=1.77338 StartY=4.98821 StartZ=0 EndX=1.89906 EndY=4.81225 EndZ=0
    g135: LineSegment StartX=1.89906 StartY=4.81225 StartZ=0 EndX=2.03312 EndY=4.72846 EndZ=0
    g136: LineSegment StartX=2.03312 StartY=4.72846 StartZ=0 EndX=2.22584 EndY=4.74522 EndZ=0
    g137: LineSegment StartX=2.22584 StartY=4.74522 StartZ=0 EndX=2.40179 EndY=4.7955 EndZ=0
    g138: LineSegment StartX=2.40179 StartY=4.7955 StartZ=0 EndX=2.55261 EndY=4.88766 EndZ=0
    g139: LineSegment StartX=2.55261 StartY=4.88766 StartZ=0 EndX=7.54655 EndY=9.895 EndZ=0
    g140: LineSegment StartX=6.93997 StartY=10.5353 StartZ=0 EndX=1.77338 EndY=5.37364 EndZ=0
    g141: LineSegment StartX=7.05801 StartY=8.12551 StartZ=0 EndX=4.38305 EndY=5.51304 EndZ=0
    g142: LineSegment StartX=4.38305 StartY=5.51304 StartZ=0 EndX=4.28305 EndY=5.27555 EndZ=0
    g143: LineSegment StartX=4.28305 StartY=5.27555 StartZ=0 EndX=4.37055 EndY=5.00055 EndZ=0
    g144: LineSegment StartX=4.37055 StartY=5.00055 StartZ=0 EndX=4.53305 EndY=4.86305 EndZ=0
    g145: LineSegment StartX=4.53305 StartY=4.86305 StartZ=0 EndX=4.84554 EndY=4.80055 EndZ=0
    g146: LineSegment StartX=4.84554 StartY=4.80055 StartZ=0 EndX=5.04554 EndY=4.90055 EndZ=0
    g147: LineSegment StartX=5.04554 StartY=4.90055 StartZ=0 EndX=7.6705 EndY=7.55051 EndZ=0
    g148: LineSegment StartX=7.6705 StartY=7.55051 StartZ=0 EndX=7.7705 EndY=7.82551 EndZ=0
    g149: LineSegment StartX=7.7705 StartY=7.82551 StartZ=0 EndX=7.683 EndY=8.01301 EndZ=0
    g150: LineSegment StartX=7.683 StartY=8.01301 StartZ=0 EndX=7.50801 EndY=8.16301 EndZ=0
    g151: LineSegment StartX=7.50801 StartY=8.16301 StartZ=0 EndX=7.33301 EndY=8.21301 EndZ=0
    g152: LineSegment StartX=7.33301 StartY=8.21301 StartZ=0 EndX=7.17051 EndY=8.18801 EndZ=0
    g153: LineSegment StartX=7.17051 StartY=8.18801 StartZ=0 EndX=7.05801 EndY=8.12551 EndZ=0
    g154: LineSegment StartX=7.0686 StartY=5.73775 StartZ=0 EndX=6.82709 EndY=5.52432 EndZ=0
    g155: LineSegment StartX=6.82709 StartY=5.52432 StartZ=0 EndX=6.73161 EndY=5.28843 EndZ=0
    g156: LineSegment StartX=6.73161 StartY=5.28843 StartZ=0 EndX=6.77093 EndY=5.01322 EndZ=0
    g157: LineSegment StartX=6.77093 StartY=5.01322 StartZ=0 EndX=6.98997 EndY=4.8391 EndZ=0
    g158: LineSegment StartX=6.98997 StartY=4.8391 StartZ=0 EndX=7.29326 EndY=4.79417 EndZ=0
    g159: LineSegment StartX=7.29326 StartY=4.79417 StartZ=0 EndX=7.48423 EndY=4.91774 EndZ=0
    g160: LineSegment StartX=7.48423 StartY=4.91774 StartZ=0 EndX=7.65272 EndY=5.12555 EndZ=0
    g161: LineSegment StartX=7.65272 StartY=5.12555 StartZ=0 EndX=7.7145 EndY=5.41761 EndZ=0
    g162: LineSegment StartX=7.7145 StartY=5.41761 StartZ=0 EndX=7.61341 EndY=5.61419 EndZ=0
    g163: LineSegment StartX=7.61341 StartY=5.61419 StartZ=0 EndX=7.49546 EndY=5.74898 EndZ=0
    g164: LineSegment StartX=7.49546 StartY=5.74898 StartZ=0 EndX=7.27641 EndY=5.74898 EndZ=0
    g165: LineSegment StartX=7.27641 StartY=5.74898 StartZ=0 EndX=7.0686 EndY=5.73775 EndZ=0
    g166: LineSegment StartX=-10.7221 StartY=14.6785 StartZ=0 EndX=-10.7221 EndY=11.6893 EndZ=0
    g167: LineSegment StartX=-10.7221 StartY=11.6893 StartZ=0 EndX=-10.5897 EndY=11.5217 EndZ=0
    g168: LineSegment StartX=-10.5897 StartY=11.5217 StartZ=0 EndX=-10.4808 EndY=11.3793 EndZ=0
    g169: LineSegment StartX=-10.4808 StartY=11.3793 StartZ=0 EndX=-10.2462 EndY=11.1782 EndZ=0
    g170: LineSegment StartX=-10.2462 StartY=11.1782 StartZ=0 EndX=4.80212 EndY=11.1782 EndZ=0
    g171: LineSegment StartX=4.80212 StartY=11.1782 StartZ=0 EndX=4.98983 EndY=11.3468 EndZ=0
    g172: LineSegment StartX=4.98983 StartY=11.3468 StartZ=0 EndX=5.0864 EndY=11.517 EndZ=0
    g173: LineSegment StartX=5.0864 StartY=11.517 StartZ=0 EndX=5.23815 EndY=11.7469 EndZ=0
    g174: LineSegment StartX=5.23815 StartY=11.7469 StartZ=0 EndX=5.23815 EndY=14.8118 EndZ=0
    g175: LineSegment StartX=5.23815 StartY=14.8118 StartZ=0 EndX=5.05397 EndY=14.8118 EndZ=0
    g176: LineSegment StartX=5.05397 StartY=14.8118 StartZ=0 EndX=5.05397 EndY=11.7954 EndZ=0
    g177: LineSegment StartX=5.05397 StartY=11.7954 StartZ=0 EndX=4.86963 EndY=11.5021 EndZ=0
    g178: LineSegment StartX=4.86963 StartY=11.5021 StartZ=0 EndX=4.70205 EndY=11.4351 EndZ=0
    g179: LineSegment StartX=4.70205 StartY=11.4351 StartZ=0 EndX=3.43684 EndY=11.4351 EndZ=0
    g180: LineSegment StartX=3.43684 StartY=11.4351 StartZ=0 EndX=3.23575 EndY=11.5524 EndZ=0
    g181: LineSegment StartX=3.23575 StartY=11.5524 StartZ=0 EndX=3.05141 EndY=11.7702 EndZ=0
    g182: LineSegment StartX=3.05141 StartY=11.7702 StartZ=0 EndX=3.05141 EndY=14.8788 EndZ=0
    g183: LineSegment StartX=3.05141 StartY=14.8788 StartZ=0 EndX=-0.97045 EndY=14.8788 EndZ=0
    g184: LineSegment StartX=-0.97045 StartY=14.8788 StartZ=0 EndX=-0.97045 EndY=11.7367 EndZ=0
    g185: LineSegment StartX=-0.97045 StartY=11.7367 StartZ=0 EndX=-1.04586 EndY=11.6194 EndZ=0
    g186: LineSegment StartX=-1.04586 StartY=11.6194 StartZ=0 EndX=-1.13803 EndY=11.544 EndZ=0
    g187: LineSegment StartX=-1.13803 StartY=11.544 StartZ=0 EndX=-1.32236 EndY=11.4267 EndZ=0
    g188: LineSegment StartX=-1.32236 StartY=11.4267 StartZ=0 EndX=-4.22682 EndY=11.4267 EndZ=0
    g189: LineSegment StartX=-4.22682 StartY=11.4267 StartZ=0 EndX=-4.46692 EndY=11.6388 EndZ=0
    g190: LineSegment StartX=-4.46692 StartY=11.6388 StartZ=0 EndX=-4.50808 EndY=11.8103 EndZ=0
    g191: LineSegment StartX=-4.50808 StartY=11.8103 StartZ=0 EndX=-4.50808 EndY=15.0287 EndZ=0
    g192: LineSegment StartX=-4.50808 StartY=15.0287 StartZ=0 EndX=-8.54336 EndY=15.0287 EndZ=0
    g193: LineSegment StartX=-8.54336 StartY=15.0287 StartZ=0 EndX=-8.54336 EndY=11.8539 EndZ=0
    g194: LineSegment StartX=-8.54336 StartY=11.8539 StartZ=0 EndX=-8.69229 EndY=11.5674 EndZ=0
    g195: LineSegment StartX=-8.69229 StartY=11.5674 StartZ=0 EndX=-8.8765 EndY=11.4139 EndZ=0
    g196: LineSegment StartX=-8.8765 StartY=11.4139 StartZ=0 EndX=-9.05394 EndY=11.4139 EndZ=0
    g197: LineSegment StartX=-9.05394 StartY=11.4139 StartZ=0 EndX=-10.2411 EndY=11.4139 EndZ=0
    g198: LineSegment StartX=-10.2411 StartY=11.4139 StartZ=0 EndX=-10.3639 EndY=11.6492 EndZ=0
    g199: LineSegment StartX=-10.3639 StartY=11.6492 StartZ=0 EndX=-10.4458 EndY=11.8642 EndZ=0
    g200: LineSegment StartX=-10.4458 StartY=11.8642 StartZ=0 EndX=-10.4458 EndY=14.7297 EndZ=0
    g201: LineSegment StartX=-10.4458 StartY=14.7297 StartZ=0 EndX=-10.7221 EndY=14.6785 EndZ=0
    g202: LineSegment StartX=-8.14874 StartY=0.829178 StartZ=0 EndX=-8.14874 EndY=3.58902 EndZ=0
    g203: LineSegment StartX=-8.14874 StartY=3.58902 StartZ=0 EndX=-7.99956 EndY=3.85008 EndZ=0
    g204: LineSegment StartX=-7.99956 StartY=3.85008 StartZ=0 EndX=-7.79444 EndY=4.01791 EndZ=0
    g205: LineSegment StartX=-7.79444 StartY=4.01791 StartZ=0 EndX=2.2566 EndY=4.01791 EndZ=0
    g206: LineSegment StartX=2.2566 StartY=4.01791 StartZ=0 EndX=2.59226 EndY=3.90603 EndZ=0
    g207: LineSegment StartX=2.59226 StartY=3.90603 StartZ=0 EndX=2.72279 EndY=3.57037 EndZ=0
    g208: LineSegment StartX=2.72279 StartY=3.57037 StartZ=0 EndX=2.72279 EndY=0.698645 EndZ=0
    g209: LineSegment StartX=2.72279 StartY=0.698645 StartZ=0 EndX=2.49902 EndY=0.51217 EndZ=0
    g210: LineSegment StartX=2.49902 StartY=0.51217 StartZ=0 EndX=-7.98091 EndY=0.51217 EndZ=0
    g211: LineSegment StartX=-7.98091 StartY=0.51217 StartZ=0 EndX=-8.14874 EndY=0.829178 EndZ=0
  constraints (236):
    c: Coincident(g0,g1)
    c: Vertical(g1)
    c: Coincident(g1,g2)
    c: Coincident(g2,g3)
    c: Coincident(g3,g4)
    c: Coincident(g4,g5)
    c: Coincident(g5,g6)
    c: Coincident(g6,g7)
    c: Coincident(g7,g8)
    c: Vertical(g8)
    c: Coincident(g8,g9)
    c: Coincident(g9,g10)
    c: Coincident(g10,g11)
    c: Coincident(g11,g12)
    c: Coincident(g12,g0)
    c: Coincident(g13,g14)
    c: Coincident(g14,g15)
    c: Coincident(g15,g16)
    c: Coincident(g16,g17)
    c: Coincident(g17,g18)
    c: Coincident(g18,g19)
    c: Horizontal(g19)
    c: Coincident(g19,g20)
    c: Coincident(g20,g21)
    c: Coincident(g21,g22)
    c: Coincident(g22,g23)
    c: Coincident(g23,g24)
    c: Coincident(g24,g25)
    c: Coincident(g25,g26)
    c: Coincident(g26,g27)
    c: Coincident(g27,g28)
    c: Coincident(g28,g13)
    c: Coincident(g29,g30)
    c: Coincident(g30,g31)
    c: Coincident(g31,g32)
    c: Coincident(g32,g33)
    c: Coincident(g33,g34)
    c: Coincident(g34,g35)
    c: Coincident(g35,g36)
    c: Coincident(g36,g37)
    c: Coincident(g37,g38)
    c: Coincident(g38,g39)
    c: Coincident(g39,g40)
    c: Coincident(g40,g41)
    c: Coincident(g41,g42)
    c: Coincident(g42,g43)
    c: Coincident(g43,g44)
    c: Coincident(g44,g29)
    c: Coincident(g60,g52)
    c: Coincident(g52,g53)
    c: Coincident(g53,g54)
    c: Coincident(g54,g55)
    c: Coincident(g55,g56)
    c: Coincident(g56,g57)
    c: Coincident(g57,g58)
    c: Coincident(g58,g59)
    c: Coincident(g59,g45)
    c: Coincident(g45,g46)
    c: Coincident(g46,g47)
    c: Coincident(g47,g48)
    c: Coincident(g48,g49)
    c: Coincident(g49,g50)
    c: Coincident(g50,g51)
    c: Coincident(g51,g60)
    c: Coincident(g75,g76)
    c: Coincident(g76,g77)
    c: Coincident(g77,g78)
    c: Coincident(g78,g79)
    c: Coincident(g79,g80)
    c: Coincident(g80,g81)
    c: Coincident(g81,g82)
    c: Coincident(g82,g83)
    c: Coincident(g83,g61)
    c: Coincident(g61,g62)
    c: Coincident(g62,g63)
    c: Coincident(g63,g64)
    c: Coincident(g64,g65)
    c: Coincident(g65,g66)
    c: Coincident(g66,g67)
    c: Coincident(g67,g75)
    c: Coincident(g92,g84)
    c: Coincident(g84,g85)
    c: Coincident(g85,g86)
    c: Coincident(g86,g87)
    c: Coincident(g87,g88)
    c: Coincident(g88,g89)
    c: Coincident(g89,g90)
    c: Coincident(g90,g91)
    c: Coincident(g91,g68)
    c: Coincident(g68,g69)
    c: Coincident(g69,g70)
    c: Coincident(g70,g71)
    c: Coincident(g71,g72)
    c: Coincident(g72,g73)
    c: Coincident(g73,g74)
    c: Coincident(g74,g92)
    c: Coincident(g122,g114)
    c: Coincident(g114,g115)
    c: Coincident(g115,g116)
    c: Coincident(g116,g117)
    c: Coincident(g117,g118)
    c: Coincident(g118,g119)
    c: Coincident(g119,g120)
    c: Coincident(g120,g121)
    c: Coincident(g121,g93)
    c: Coincident(g93,g94)
    c: Coincident(g94,g95)
    c: Coincident(g95,g96)
    c: Coincident(g96,g97)
    c: Coincident(g97,g98)
    c: Coincident(g98,g99)
    c: Coincident(g99,g122)
    c: Coincident(g123,g124)
    c: Coincident(g124,g125)
    c: Coincident(g125,g126)
    c: Coincident(g126,g127)
    c: Coincident(g127,g128)
    c: Coincident(g128,g129)
    c: Coincident(g129,g130)
    c: Coincident(g130,g131)
    c: Coincident(g131,g100)
    c: Coincident(g100,g101)
    c: Coincident(g101,g102)
    c: Coincident(g102,g103)
    c: Coincident(g103,g104)
    c: Coincident(g104,g105)
    c: Coincident(g105,g106)
    c: Coincident(g106,g123)
    c: Coincident(g140,g132)
    c: Coincident(g132,g133)
    c: Coincident(g133,g134)
    c: Coincident(g134,g135)
    c: Coincident(g135,g136)
    c: Coincident(g136,g137)
    c: Coincident(g137,g138)
    c: Coincident(g138,g139)
    c: Coincident(g139,g107)
    c: Coincident(g107,g108)
    c: Coincident(g108,g109)
    c: Coincident(g109,g110)
    c: Coincident(g110,g111)
    c: Coincident(g111,g112)
    c: Coincident(g112,g113)
    c: Coincident(g113,g140)
    c: Coincident(g141,g142)
    c: Coincident(g142,g143)
    c: Coincident(g143,g144)
    c: Coincident(g144,g145)
    c: Coincident(g145,g146)
    c: Coincident(g146,g147)
    c: Coincident(g147,g148)
    c: Coincident(g148,g149)
    c: Coincident(g149,g150)
    c: Coincident(g150,g151)
    c: Coincident(g151,g152)
    c: Coincident(g152,g153)
    c: Coincident(g153,g141)
    c: Coincident(g154,g155)
    c: Coincident(g155,g156)
    c: Coincident(g156,g157)
    c: Coincident(g157,g158)
    c: Coincident(g158,g159)
    c: Coincident(g159,g160)
    c: Coincident(g160,g161)
    c: Coincident(g161,g162)
    c: Coincident(g162,g163)
    c: Coincident(g163,g164)
    c: Horizontal(g164)
    c: Coincident(g164,g165)
    c: Coincident(g165,g154)
    c: Vertical(g166)
    c: Coincident(g166,g167)
    c: Coincident(g167,g168)
    c: Coincident(g168,g169)
    c: Coincident(g169,g170)
    c: Horizontal(g170)
    c: Coincident(g170,g171)
    c: Coincident(g171,g172)
    c: Coincident(g172,g173)
    c: Coincident(g173,g174)
    c: Vertical(g174)
    c: Coincident(g174,g175)
    c: Horizontal(g175)
    c: Coincident(g175,g176)
    c: Vertical(g176)
    c: Coincident(g176,g177)
    c: Coincident(g177,g178)
    c: Coincident(g178,g179)
    c: Horizontal(g179)
    c: Coincident(g179,g180)
    c: Coincident(g180,g181)
    c: Coincident(g181,g182)
    c: Vertical(g182)
    c: Coincident(g182,g183)
    c: Horizontal(g183)
    c: Coincident(g183,g184)
    c: Vertical(g184)
    c: Coincident(g184,g185)
    c: Coincident(g185,g186)
    c: Coincident(g186,g187)
    c: Coincident(g187,g188)
    c: Horizontal(g188)
    c: Coincident(g188,g189)
    c: Coincident(g189,g190)
    c: Coincident(g190,g191)
    c: Vertical(g191)
    c: Coincident(g191,g192)
    c: Horizontal(g192)
    c: Coincident(g192,g193)
    c: Vertical(g193)
    c: Coincident(g193,g194)
    c: Coincident(g194,g195)
    c: Coincident(g195,g196)
    c: Horizontal(g196)
    c: Coincident(g196,g197)
    c: Horizontal(g197)
    c: Coincident(g197,g198)
    c: Coincident(g198,g199)
    c: Coincident(g199,g200)
    c: Vertical(g200)
    c: Coincident(g200,g201)
    c: Coincident(g201,g166)
    c: Vertical(g202)
    c: Coincident(g202,g203)
    c: Coincident(g203,g204)
    c: Coincident(g204,g205)
    c: Horizontal(g205)
    c: Coincident(g205,g206)
    c: Coincident(g206,g207)
    c: Coincident(g207,g208)
    c: Vertical(g208)
    c: Coincident(g208,g209)
    c: Coincident(g209,g210)
    c: Horizontal(g210)
    c: Coincident(g210,g211)
    c: Coincident(g211,g202)
FEATURE [PartDesign::Pocket] Pocket003
  BaseFeature = -> Pocket002
  Length = 0.1
  Length2 = 100
  Profile = -> Sketch007
  Type = 0
FEATURE [Image::ImagePlane] ImagePlane002
  Placement = pos=(-2.8,0,5.6) rot=(1,0,0;4.71239rad)
  XSize = 41.59
  YSize = 26.21
FEATURE [Sketcher::SketchObject] Sketch008
  FullyConstrained = false
  MapMode = 5
  Placement = pos=(0,17.4805,0) rot=(0,0.707107,0.707107;3.14159rad)
  Support = -> [Pocket003]
  sketch-geometry (149):
    g0: LineSegment StartX=-0.25893 StartY=12.4541 StartZ=0 EndX=-7.39517 EndY=4.91425 EndZ=0
    g1: LineSegment StartX=-7.39517 StartY=4.91425 StartZ=0 EndX=-7.52239 EndY=4.64223 EndZ=0
    g2: LineSegment StartX=-7.52239 StartY=4.64223 StartZ=0 EndX=-7.49848 EndY=4.46295 EndZ=0
    g3: LineSegment StartX=-7.49848 StartY=4.46295 StartZ=0 EndX=-7.38097 EndY=4.22851 EndZ=0
    g4: LineSegment StartX=-7.38097 StartY=4.22851 StartZ=0 EndX=-7.20579 EndY=4.11172 EndZ=0
    g5: LineSegment StartX=-7.20579 StartY=4.11172 StartZ=0 EndX=-6.92113 EndY=4.11172 EndZ=0
    g6: LineSegment StartX=-6.92113 StartY=4.11172 StartZ=0 EndX=-6.67296 EndY=4.19202 EndZ=0
    g7: LineSegment StartX=-6.67296 StartY=4.19202 StartZ=0 EndX=0.472111 EndY=11.7498 EndZ=0
    g8: LineSegment StartX=0.472111 StartY=11.7498 StartZ=0 EndX=0.543433 EndY=12.0618 EndZ=0
    g9: LineSegment StartX=0.543433 StartY=12.0618 StartZ=0 EndX=0.472111 EndY=12.3114 EndZ=0
    g10: LineSegment StartX=0.472111 StartY=12.3114 StartZ=0 EndX=0.400791 EndY=12.4808 EndZ=0
    g11: LineSegment StartX=0.400791 StartY=12.4808 StartZ=0 EndX=0.231403 EndY=12.561 EndZ=0
    g12: LineSegment StartX=0.231403 StartY=12.561 StartZ=0 EndX=0 EndY=12.5789 EndZ=0
    g13: LineSegment StartX=0 StartY=12.5789 StartZ=0 EndX=-0.151948 EndY=12.5432 EndZ=0
    g14: LineSegment StartX=-0.151948 StartY=12.5432 StartZ=0 EndX=-0.25893 EndY=12.4541 EndZ=0
    g15: LineSegment StartX=2.1265 StartY=12.4411 StartZ=0 EndX=-5.00975 EndY=4.90126 EndZ=0
    g16: LineSegment StartX=-5.00975 StartY=4.90126 StartZ=0 EndX=-5.13696 EndY=4.62923 EndZ=0
    g17: LineSegment StartX=-5.13696 StartY=4.62923 StartZ=0 EndX=-5.11306 EndY=4.44995 EndZ=0
    g18: LineSegment StartX=-5.11306 StartY=4.44995 StartZ=0 EndX=-4.99554 EndY=4.21552 EndZ=0
    g19: LineSegment StartX=-4.99554 StartY=4.21552 StartZ=0 EndX=-4.82037 EndY=4.09873 EndZ=0
    g20: LineSegment StartX=-4.82037 StartY=4.09873 StartZ=0 EndX=-4.5357 EndY=4.09873 EndZ=0
    g21: LineSegment StartX=-4.5357 StartY=4.09873 StartZ=0 EndX=-4.28753 EndY=4.17902 EndZ=0
    g22: LineSegment StartX=-4.28753 StartY=4.17902 StartZ=0 EndX=2.85754 EndY=11.7368 EndZ=0
    g23: LineSegment StartX=2.85754 StartY=11.7368 StartZ=0 EndX=2.92886 EndY=12.0488 EndZ=0
    g24: LineSegment StartX=2.92886 StartY=12.0488 StartZ=0 EndX=2.85754 EndY=12.2984 EndZ=0
    g25: LineSegment StartX=2.85754 StartY=12.2984 StartZ=0 EndX=2.78622 EndY=12.4678 EndZ=0
    g26: LineSegment StartX=2.78622 StartY=12.4678 StartZ=0 EndX=2.61683 EndY=12.548 EndZ=0
    g27: LineSegment StartX=2.61683 StartY=12.548 StartZ=0 EndX=2.38543 EndY=12.5659 EndZ=0
    g28: LineSegment StartX=2.38543 StartY=12.5659 StartZ=0 EndX=2.23348 EndY=12.5302 EndZ=0
    g29: LineSegment StartX=2.23348 StartY=12.5302 StartZ=0 EndX=2.1265 EndY=12.4411 EndZ=0
    g30: LineSegment StartX=-2.23731 StartY=4.19119 StartZ=0 EndX=-1.95264 EndY=4.19119 EndZ=0
    g31: LineSegment StartX=-1.95264 StartY=4.19119 StartZ=0 EndX=-1.70447 EndY=4.27148 EndZ=0
    g32: LineSegment StartX=-1.70447 StartY=4.27148 StartZ=0 EndX=5.4406 EndY=11.8292 EndZ=0
    g33: LineSegment StartX=5.4406 StartY=11.8292 StartZ=0 EndX=5.51192 EndY=12.1412 EndZ=0
    g34: LineSegment StartX=5.51192 StartY=12.1412 StartZ=0 EndX=5.4406 EndY=12.3909 EndZ=0
    g35: LineSegment StartX=5.4406 StartY=12.3909 StartZ=0 EndX=5.36928 EndY=12.5603 EndZ=0
    g36: LineSegment StartX=5.36928 StartY=12.5603 StartZ=0 EndX=5.19989 EndY=12.6405 EndZ=0
    g37: LineSegment StartX=5.19989 StartY=12.6405 StartZ=0 EndX=4.96849 EndY=12.6583 EndZ=0
    g38: LineSegment StartX=4.96849 StartY=12.6583 StartZ=0 EndX=4.81654 EndY=12.6227 EndZ=0
    g39: LineSegment StartX=4.81654 StartY=12.6227 StartZ=0 EndX=4.70956 EndY=12.5335 EndZ=0
    g40: LineSegment StartX=7.09498 StartY=12.5205 StartZ=0 EndX=-0.041257 EndY=4.98072 EndZ=0
    g41: LineSegment StartX=-0.041257 StartY=4.98072 StartZ=0 EndX=-0.168473 EndY=4.7087 EndZ=0
    g42: LineSegment StartX=-0.168473 StartY=4.7087 StartZ=0 EndX=-0.144569 EndY=4.52942 EndZ=0
    g43: LineSegment StartX=-0.144569 StartY=4.52942 StartZ=0 EndX=-0.027057 EndY=4.29498 EndZ=0
    g44: LineSegment StartX=-0.027057 StartY=4.29498 StartZ=0 EndX=0.148122 EndY=4.17819 EndZ=0
    g45: LineSegment StartX=0.148122 StartY=4.17819 StartZ=0 EndX=0.432787 EndY=4.17819 EndZ=0
    g46: LineSegment StartX=0.432787 StartY=4.17819 StartZ=0 EndX=0.680957 EndY=4.25849 EndZ=0
    g47: LineSegment StartX=0.680957 StartY=4.25849 StartZ=0 EndX=7.82603 EndY=11.8162 EndZ=0
    g48: LineSegment StartX=7.82603 StartY=11.8162 StartZ=0 EndX=7.89735 EndY=12.1283 EndZ=0
    g49: LineSegment StartX=7.89735 StartY=12.1283 StartZ=0 EndX=7.82603 EndY=12.3779 EndZ=0
    g50: LineSegment StartX=7.82603 StartY=12.3779 StartZ=0 EndX=7.75471 EndY=12.5473 EndZ=0
    g51: LineSegment StartX=7.75471 StartY=12.5473 StartZ=0 EndX=7.58532 EndY=12.6275 EndZ=0
    g52: LineSegment StartX=7.58532 StartY=12.6275 StartZ=0 EndX=7.35391 EndY=12.6453 EndZ=0
    g53: LineSegment StartX=7.35391 StartY=12.6453 StartZ=0 EndX=7.20197 EndY=12.6097 EndZ=0
    g54: LineSegment StartX=7.20197 StartY=12.6097 StartZ=0 EndX=7.09498 EndY=12.5205 EndZ=0
    g55: LineSegment StartX=4.70956 StartY=12.5335 StartZ=0 EndX=-2.42668 EndY=4.99372 EndZ=0
    g56: LineSegment StartX=-2.42668 StartY=4.99372 StartZ=0 EndX=-2.5539 EndY=4.72169 EndZ=0
    g57: LineSegment StartX=-2.5539 StartY=4.72169 StartZ=0 EndX=-2.53 EndY=4.54241 EndZ=0
    g58: LineSegment StartX=-2.53 StartY=4.54241 StartZ=0 EndX=-2.41248 EndY=4.30797 EndZ=0
    g59: LineSegment StartX=-2.41248 StartY=4.30797 StartZ=0 EndX=-2.23731 EndY=4.19119 EndZ=0
    g60: LineSegment StartX=10.369 StartY=11.782 StartZ=0 EndX=10.4404 EndY=12.094 EndZ=0
    g61: LineSegment StartX=10.4404 StartY=12.094 StartZ=0 EndX=10.369 EndY=12.3436 EndZ=0
    g62: LineSegment StartX=10.369 StartY=12.3436 StartZ=0 EndX=10.2977 EndY=12.513 EndZ=0
    g63: LineSegment StartX=10.2977 StartY=12.513 StartZ=0 EndX=10.1283 EndY=12.5932 EndZ=0
    g64: LineSegment StartX=10.1283 StartY=12.5932 StartZ=0 EndX=9.89693 EndY=12.6111 EndZ=0
    g65: LineSegment StartX=9.89693 StartY=12.6111 StartZ=0 EndX=9.74498 EndY=12.5754 EndZ=0
    g66: LineSegment StartX=9.74498 StartY=12.5754 StartZ=0 EndX=9.638 EndY=12.4863 EndZ=0
    g67: LineSegment StartX=12.7545 StartY=11.769 StartZ=0 EndX=12.8258 EndY=12.081 EndZ=0
    g68: LineSegment StartX=12.8258 StartY=12.081 StartZ=0 EndX=12.7545 EndY=12.3306 EndZ=0
    g69: LineSegment StartX=12.7545 StartY=12.3306 StartZ=0 EndX=12.6831 EndY=12.5 EndZ=0
    g70: LineSegment StartX=12.6831 StartY=12.5 StartZ=0 EndX=12.5138 EndY=12.5803 EndZ=0
    g71: LineSegment StartX=12.5138 StartY=12.5803 StartZ=0 EndX=12.2824 EndY=12.5981 EndZ=0
    g72: LineSegment StartX=12.2824 StartY=12.5981 StartZ=0 EndX=12.1304 EndY=12.5624 EndZ=0
    g73: LineSegment StartX=12.1304 StartY=12.5624 StartZ=0 EndX=12.0234 EndY=12.4733 EndZ=0
    g74: LineSegment StartX=2.69114 StartY=4.14394 StartZ=0 EndX=2.9758 EndY=4.14394 EndZ=0
    g75: LineSegment StartX=2.9758 StartY=4.14394 StartZ=0 EndX=3.22397 EndY=4.22423 EndZ=0
    g76: LineSegment StartX=3.22397 StartY=4.22423 StartZ=0 EndX=10.369 EndY=11.782 EndZ=0
    g77: LineSegment StartX=12.0234 StartY=12.4733 StartZ=0 EndX=4.88718 EndY=4.93347 EndZ=0
    g78: LineSegment StartX=4.88718 StartY=4.93347 StartZ=0 EndX=4.75997 EndY=4.66145 EndZ=0
    g79: LineSegment StartX=4.75997 StartY=4.66145 StartZ=0 EndX=4.78387 EndY=4.48217 EndZ=0
    g80: LineSegment StartX=4.78387 StartY=4.48217 StartZ=0 EndX=4.90138 EndY=4.24773 EndZ=0
    g81: LineSegment StartX=4.90138 StartY=4.24773 StartZ=0 EndX=5.07656 EndY=4.13095 EndZ=0
    g82: LineSegment StartX=5.07656 StartY=4.13095 StartZ=0 EndX=5.36123 EndY=4.13095 EndZ=0
    g83: LineSegment StartX=5.36123 StartY=4.13095 StartZ=0 EndX=5.6094 EndY=4.21124 EndZ=0
    g84: LineSegment StartX=5.6094 StartY=4.21124 StartZ=0 EndX=12.7545 EndY=11.769 EndZ=0
    g85: LineSegment StartX=9.638 StartY=12.4863 StartZ=0 EndX=2.50176 EndY=4.94647 EndZ=0
    g86: LineSegment StartX=2.50176 StartY=4.94647 StartZ=0 EndX=2.37454 EndY=4.67444 EndZ=0
    g87: LineSegment StartX=2.37454 StartY=4.67444 StartZ=0 EndX=2.39844 EndY=4.49516 EndZ=0
    g88: LineSegment StartX=2.39844 StartY=4.49516 StartZ=0 EndX=2.51596 EndY=4.26073 EndZ=0
    g89: LineSegment StartX=2.51596 StartY=4.26073 StartZ=0 EndX=2.69114 EndY=4.14394 EndZ=0
    g90: LineSegment StartX=-2.68453 StartY=12.4971 StartZ=0 EndX=-7.44332 EndY=7.52786 EndZ=0
    g91: LineSegment StartX=-7.44332 StartY=7.52786 StartZ=0 EndX=-7.50573 EndY=7.21583 EndZ=0
    g92: LineSegment StartX=-7.50573 StartY=7.21583 StartZ=0 EndX=-7.42549 EndY=6.94838 EndZ=0
    g93: LineSegment StartX=-7.42549 StartY=6.94838 StartZ=0 EndX=-7.18478 EndY=6.7255 EndZ=0
    g94: LineSegment StartX=-7.18478 StartY=6.7255 StartZ=0 EndX=-6.91733 EndY=6.7255 EndZ=0
    g95: LineSegment StartX=-6.91733 StartY=6.7255 StartZ=0 EndX=-6.6677 EndY=6.8414 EndZ=0
    g96: LineSegment StartX=-6.6677 StartY=6.8414 StartZ=0 EndX=-1.95304 EndY=11.8055 EndZ=0
    g97: LineSegment StartX=-1.95304 StartY=11.8055 StartZ=0 EndX=-1.87324 EndY=12.1114 EndZ=0
    g98: LineSegment StartX=-1.87324 StartY=12.1114 StartZ=0 EndX=-2.03284 EndY=12.3907 EndZ=0
    g99: LineSegment StartX=-2.03284 StartY=12.3907 StartZ=0 EndX=-2.24563 EndY=12.537 EndZ=0
    g100: LineSegment StartX=-2.24563 StartY=12.537 StartZ=0 EndX=-2.45843 EndY=12.537 EndZ=0
    g101: LineSegment StartX=-2.45843 StartY=12.537 StartZ=0 EndX=-2.68453 EndY=12.4971 EndZ=0
    g102: LineSegment StartX=12.9546 StartY=9.16229 StartZ=0 EndX=13.0344 EndY=9.46819 EndZ=0
    g103: LineSegment StartX=13.0344 StartY=9.46819 StartZ=0 EndX=12.8748 EndY=9.74749 EndZ=0
    g104: LineSegment StartX=12.8748 StartY=9.74749 StartZ=0 EndX=12.6621 EndY=9.89378 EndZ=0
    g105: LineSegment StartX=12.6621 StartY=9.89378 StartZ=0 EndX=12.4493 EndY=9.89378 EndZ=0
    g106: LineSegment StartX=12.4493 StartY=9.89378 StartZ=0 EndX=12.2232 EndY=9.85388 EndZ=0
    g107: LineSegment StartX=7.46436 StartY=4.88461 StartZ=0 EndX=7.40196 EndY=4.57258 EndZ=0
    g108: LineSegment StartX=7.40196 StartY=4.57258 StartZ=0 EndX=7.48219 EndY=4.30513 EndZ=0
    g109: LineSegment StartX=7.48219 StartY=4.30513 StartZ=0 EndX=7.7229 EndY=4.08225 EndZ=0
    g110: LineSegment StartX=7.7229 StartY=4.08225 StartZ=0 EndX=7.99036 EndY=4.08225 EndZ=0
    g111: LineSegment StartX=7.99036 StartY=4.08225 StartZ=0 EndX=8.23998 EndY=4.19814 EndZ=0
    g112: LineSegment StartX=12.2232 StartY=9.85388 StartZ=0 EndX=7.46436 EndY=4.88461 EndZ=0
    g113: LineSegment StartX=8.23998 StartY=4.19814 StartZ=0 EndX=12.9546 EndY=9.16229 EndZ=0
    g114: LineSegment StartX=-5.09526 StartY=12.5289 StartZ=0 EndX=-4.76902 EndY=12.6076 EndZ=0
    g115: LineSegment StartX=-4.76902 StartY=12.6076 StartZ=0 EndX=-4.58981 EndY=12.5626 EndZ=0
    g116: LineSegment StartX=-4.58981 StartY=12.5626 StartZ=0 EndX=-4.47029 EndY=12.4072 EndZ=0
    g117: LineSegment StartX=-4.47029 StartY=12.4072 StartZ=0 EndX=-4.35212 EndY=12.1926 EndZ=0
    g118: LineSegment StartX=-4.35212 StartY=12.1926 StartZ=0 EndX=-4.37005 EndY=11.9416 EndZ=0
    g119: LineSegment StartX=-4.37005 StartY=11.9416 StartZ=0 EndX=-4.45372 EndY=11.7085 EndZ=0
    g120: LineSegment StartX=-4.45372 StartY=11.7085 StartZ=0 EndX=-6.85084 EndY=9.28375 EndZ=0
    g121: LineSegment StartX=-6.85084 StartY=9.28375 StartZ=0 EndX=-7.17004 EndY=9.31035 EndZ=0
    g122: LineSegment StartX=-7.17004 StartY=9.31035 StartZ=0 EndX=-7.38284 EndY=9.50985 EndZ=0
    g123: LineSegment StartX=-7.38284 StartY=9.50985 StartZ=0 EndX=-7.46263 EndY=9.82904 EndZ=0
    g124: LineSegment StartX=-7.46263 StartY=9.82904 StartZ=0 EndX=-7.40943 EndY=10.1615 EndZ=0
    g125: LineSegment StartX=-7.40943 StartY=10.1615 StartZ=0 EndX=-5.09526 EndY=12.5289 EndZ=0
    g126: LineSegment StartX=12.2482 StartY=7.23819 StartZ=0 EndX=12.5745 EndY=7.31685 EndZ=0
    g127: LineSegment StartX=12.5745 StartY=7.31685 StartZ=0 EndX=12.7537 EndY=7.27183 EndZ=0
    g128: LineSegment StartX=12.7537 StartY=7.27183 StartZ=0 EndX=12.8732 EndY=7.11646 EndZ=0
    g129: LineSegment StartX=12.8732 StartY=7.11646 StartZ=0 EndX=12.9914 EndY=6.90184 EndZ=0
    g130: LineSegment StartX=12.9914 StartY=6.90184 StartZ=0 EndX=12.9734 EndY=6.65085 EndZ=0
    g131: LineSegment StartX=12.9734 StartY=6.65085 StartZ=0 EndX=12.8898 EndY=6.41779 EndZ=0
    g132: LineSegment StartX=10.4927 StartY=3.99302 StartZ=0 EndX=10.1735 EndY=4.01962 EndZ=0
    g133: LineSegment StartX=10.1735 StartY=4.01962 StartZ=0 EndX=9.96067 EndY=4.21912 EndZ=0
    g134: LineSegment StartX=9.96067 StartY=4.21912 StartZ=0 EndX=9.88087 EndY=4.53831 EndZ=0
    g135: LineSegment StartX=9.88087 StartY=4.53831 StartZ=0 EndX=9.93407 EndY=4.87081 EndZ=0
    g136: LineSegment StartX=12.8898 StartY=6.41779 StartZ=0 EndX=10.4927 EndY=3.99302 EndZ=0
    g137: LineSegment StartX=9.93407 StartY=4.87081 StartZ=0 EndX=12.2482 EndY=7.23819 EndZ=0
    g138: LineSegment StartX=-8.43224 StartY=-1.18841 StartZ=0 EndX=-7.89264 EndY=-0.31198 EndZ=0
    g139: LineSegment StartX=-7.89264 StartY=-0.31198 StartZ=0 EndX=-7.89264 EndY=2.36836 EndZ=0
    g140: LineSegment StartX=-7.89264 StartY=2.36836 StartZ=0 EndX=-7.64897 EndY=2.75823 EndZ=0
    g141: LineSegment StartX=-7.64897 StartY=2.75823 StartZ=0 EndX=-7.43779 EndY=3.01814 EndZ=0
    g142: LineSegment StartX=-7.43779 StartY=3.01814 StartZ=0 EndX=-7.19412 EndY=3.21308 EndZ=0
    g143: LineSegment StartX=-7.19412 StartY=3.21308 StartZ=0 EndX=12.6028 EndY=3.21308 EndZ=0
    g144: LineSegment StartX=12.6028 StartY=3.21308 StartZ=0 EndX=12.9663 EndY=3.0283 EndZ=0
    g145: LineSegment StartX=12.9663 StartY=3.0283 StartZ=0 EndX=13.2329 EndY=2.66479 EndZ=0
    g146: LineSegment StartX=13.2329 StartY=2.66479 StartZ=0 EndX=13.4268 EndY=2.32552 EndZ=0
    g147: LineSegment StartX=13.4268 StartY=2.32552 StartZ=0 EndX=13.4268 EndY=-1.18841 EndZ=0
    g148: LineSegment StartX=13.4268 StartY=-1.18841 StartZ=0 EndX=-8.43224 EndY=-1.18841 EndZ=0
  constraints (164):
    c: Coincident(g0,g1)
    c: Coincident(g1,g2)
    c: Coincident(g2,g3)
    c: Coincident(g3,g4)
    c: Coincident(g4,g5)
    c: Horizontal(g5)
    c: Coincident(g5,g6)
    c: Coincident(g6,g7)
    c: Coincident(g7,g8)
    c: Coincident(g8,g9)
    c: Coincident(g9,g10)
    c: Coincident(g10,g11)
    c: Coincident(g11,g12)
    c: PointOnObject(g12,g-2)
    c: Coincident(g12,g13)
    c: Coincident(g13,g14)
    c: Coincident(g14,g0)
    c: Coincident(g15,g16)
    c: Coincident(g16,g17)
    c: Coincident(g17,g18)
    c: Coincident(g18,g19)
    c: Coincident(g19,g20)
    c: Horizontal(g20)
    c: Coincident(g20,g21)
    c: Coincident(g21,g22)
    c: Coincident(g22,g23)
    c: Coincident(g23,g24)
    c: Coincident(g24,g25)
    c: Coincident(g25,g26)
    c: Coincident(g26,g27)
    c: Coincident(g27,g28)
    c: Coincident(g28,g29)
    c: Coincident(g29,g15)
    c: Coincident(g55,g56)
    c: Coincident(g56,g57)
    c: Coincident(g57,g58)
    c: Coincident(g58,g59)
    c: Coincident(g59,g30)
    c: Horizontal(g30)
    c: Coincident(g30,g31)
    c: Coincident(g31,g32)
    c: Coincident(g32,g33)
    c: Coincident(g33,g34)
    c: Coincident(g34,g35)
    c: Coincident(g35,g36)
    c: Coincident(g36,g37)
    c: Coincident(g37,g38)
    c: Coincident(g38,g39)
    c: Coincident(g39,g55)
    c: Coincident(g40,g41)
    c: Coincident(g41,g42)
    c: Coincident(g42,g43)
    c: Coincident(g43,g44)
    c: Coincident(g44,g45)
    c: Horizontal(g45)
    c: Coincident(g45,g46)
    c: Coincident(g46,g47)
    c: Coincident(g47,g48)
    c: Coincident(g48,g49)
    c: Coincident(g49,g50)
    c: Coincident(g50,g51)
    c: Coincident(g51,g52)
    c: Coincident(g52,g53)
    c: Coincident(g53,g54)
    c: Coincident(g54,g40)
    c: Coincident(g85,g86)
    c: Coincident(g86,g87)
    c: Coincident(g87,g88)
    c: Coincident(g88,g89)
    c: Coincident(g89,g74)
    c: Horizontal(g74)
    c: Coincident(g74,g75)
    c: Coincident(g75,g76)
    c: Coincident(g76,g60)
    c: Coincident(g60,g61)
    c: Coincident(g61,g62)
    c: Coincident(g62,g63)
    c: Coincident(g63,g64)
    c: Coincident(g64,g65)
    c: Coincident(g65,g66)
    c: Coincident(g66,g85)
    c: Coincident(g77,g78)
    c: Coincident(g78,g79)
    c: Coincident(g79,g80)
    c: Coincident(g80,g81)
    c: Coincident(g81,g82)
    c: Horizontal(g82)
    c: Coincident(g82,g83)
    c: Coincident(g83,g84)
    c: Coincident(g84,g67)
    c: Coincident(g67,g68)
    c: Coincident(g68,g69)
    c: Coincident(g69,g70)
    c: Coincident(g70,g71)
    c: Coincident(g71,g72)
    c: Coincident(g72,g73)
    c: Coincident(g73,g77)
    c: Coincident(g90,g91)
    c: Coincident(g91,g92)
    c: Coincident(g92,g93)
    c: Coincident(g93,g94)
    c: Horizontal(g94)
    c: Coincident(g94,g95)
    c: Coincident(g95,g96)
    c: Coincident(g96,g97)
    c: Coincident(g97,g98)
    c: Coincident(g98,g99)
    c: Coincident(g99,g100)
    c: Horizontal(g100)
    c: Coincident(g100,g101)
    c: Coincident(g101,g90)
    c: Coincident(g112,g107)
    c: Coincident(g107,g108)
    c: Coincident(g108,g109)
    c: Coincident(g109,g110)
    c: Horizontal(g110)
    c: Coincident(g110,g111)
    c: Coincident(g111,g113)
    c: Coincident(g113,g102)
    c: Coincident(g102,g103)
    c: Coincident(g103,g104)
    c: Coincident(g104,g105)
    c: Horizontal(g105)
    c: Coincident(g105,g106)
    c: Coincident(g106,g112)
    c: Coincident(g114,g115)
    c: Coincident(g115,g116)
    c: Coincident(g116,g117)
    c: Coincident(g117,g118)
    c: Coincident(g118,g119)
    c: Coincident(g119,g120)
    c: Coincident(g120,g121)
    c: Coincident(g121,g122)
    c: Coincident(g122,g123)
    c: Coincident(g123,g124)
    c: Coincident(g124,g125)
    c: Coincident(g125,g114)
    c: Coincident(g126,g127)
    c: Coincident(g127,g128)
    c: Coincident(g128,g129)
    c: Coincident(g129,g130)
    c: Coincident(g130,g131)
    c: Coincident(g131,g136)
    c: Coincident(g136,g132)
    c: Coincident(g132,g133)
    c: Coincident(g133,g134)
    c: Coincident(g134,g135)
    c: Coincident(g135,g137)
    c: Coincident(g137,g126)
    c: Coincident(g138,g139)
    c: Vertical(g139)
    c: Coincident(g139,g140)
    c: Coincident(g140,g141)
    c: Coincident(g141,g142)
    c: Coincident(g142,g143)
    c: Horizontal(g143)
    c: Coincident(g143,g144)
    c: Coincident(g144,g145)
    c: Coincident(g145,g146)
    c: Coincident(g146,g147)
    c: Vertical(g147)
    c: Coincident(g147,g148)
    c: Coincident(g148,g138)
    c: Horizontal(g148)
FEATURE [PartDesign::Pocket] Pocket004
  BaseFeature = -> Pocket003
  Length = 0.1
  Length2 = 100
  Profile = -> Sketch008
  Type = 0
FEATURE [Sketcher::SketchObject] Sketch009
  FullyConstrained = false
  MapMode = 5
  Placement = pos=(0,17.3805,0) rot=(0,0.707107,0.707107;3.14159rad)
  Support = -> [Pocket004]
  sketch-geometry (4):
    g0: LineSegment StartX=-3.04449 StartY=3.05673 StartZ=0 EndX=8.66046 EndY=3.05673 EndZ=0
    g1: LineSegment StartX=8.66046 StartY=3.05673 StartZ=0 EndX=8.66046 EndY=1.50577 EndZ=0
    g2: LineSegment StartX=8.66046 StartY=1.50577 StartZ=0 EndX=-3.04449 EndY=1.50577 EndZ=0
    g3: LineSegment StartX=-3.04449 StartY=1.50577 StartZ=0 EndX=-3.04449 EndY=3.05673 EndZ=0
  constraints (8):
    c: Coincident(g0,g1)
    c: Coincident(g1,g2)
    c: Coincident(g2,g3)
    c: Coincident(g3,g0)
    c: Horizontal(g0)
    c: Horizontal(g2)
    c: Vertical(g1)
    c: Vertical(g3)
FEATURE [PartDesign::Pocket] Pocket005
  BaseFeature = -> Pocket004
  Length = 0.1
  Length2 = 100
  Profile = -> Sketch009
  Type = 0
FEATURE [Image::ImagePlane] ImagePlane003
  Placement = pos=(0,-10.5,18) rot=(-0.57735,0.57735,0.57735;4.18879rad)
  XSize = 74
  YSize = 71
FEATURE [Sketcher::SketchObject] Sketch010
  FullyConstrained = false
  MapMode = 5
  Placement = pos=(-17.9389,0,0) rot=(0.57735,-0.57735,-0.57735;2.0944rad)
  Support = -> [Pocket005]
  sketch-geometry (56):
    g0: ArcOfCircle CenterX=2.05756 CenterY=1.70026 CenterZ=0 NormalX=0 NormalY=0 NormalZ=1 AngleXU=0 Radius=1.61933 StartAngle=1.5708 EndAngle=4.71239
    g1: ArcOfCircle CenterX=8.03375 CenterY=1.70026 CenterZ=0 NormalX=0 NormalY=0 NormalZ=1 AngleXU=0 Radius=1.61933 StartAngle=4.71239 EndAngle=7.85398
    g2: LineSegment StartX=2.05756 StartY=0.080924 StartZ=0 EndX=8.03375 EndY=0.080924 EndZ=0
    g3: LineSegment StartX=2.05756 StartY=3.31959 StartZ=0 EndX=8.03375 EndY=3.31959 EndZ=0
    g4: ArcOfCircle CenterX=-5.01528 CenterY=6.91658 CenterZ=0 NormalX=0 NormalY=0 NormalZ=1 AngleXU=0 Radius=0.842181 StartAngle=1.5708 EndAngle=4.71239
    g5: ArcOfCircle CenterX=6.22245 CenterY=6.91658 CenterZ=0 NormalX=0 NormalY=0 NormalZ=1 AngleXU=0 Radius=0.842181 StartAngle=4.71239 EndAngle=7.85398
    g6: LineSegment StartX=-5.01528 StartY=6.0744 StartZ=0 EndX=6.22245 EndY=6.0744 EndZ=0
    g7: LineSegment StartX=-5.01528 StartY=7.75876 StartZ=0 EndX=6.22245 EndY=7.75876 EndZ=0
    g8: ArcOfCircle CenterX=-10.9035 CenterY=10.8823 CenterZ=0 NormalX=0 NormalY=0 NormalZ=1 AngleXU=0 Radius=0.462832 StartAngle=0.759527 EndAngle=3.90112
    g9: ArcOfCircle CenterX=-8.74642 CenterY=8.61063 CenterZ=0 NormalX=0 NormalY=0 NormalZ=1 AngleXU=0 Radius=0.462832 StartAngle=3.90112 EndAngle=7.04271
    g10: LineSegment StartX=-11.2391 StartY=10.5636 StartZ=0 EndX=-9.08205 EndY=8.29193 EndZ=0
    g11: LineSegment StartX=-10.5679 StartY=11.201 StartZ=0 EndX=-8.41079 EndY=8.92933 EndZ=0
    g12: ArcOfCircle CenterX=-8.48343 CenterY=10.8779 CenterZ=0 NormalX=0 NormalY=0 NormalZ=1 AngleXU=0 Radius=0.462832 StartAngle=0.759527 EndAngle=3.90112
    g13: ArcOfCircle CenterX=-6.32638 CenterY=8.60621 CenterZ=0 NormalX=0 NormalY=0 NormalZ=1 AngleXU=0 Radius=0.462832 StartAngle=3.90112 EndAngle=7.04271
    g14: LineSegment StartX=-8.81906 StartY=10.5592 StartZ=0 EndX=-6.662 EndY=8.28751 EndZ=0
    g15: LineSegment StartX=-8.1478 StartY=11.1966 StartZ=0 EndX=-5.99075 EndY=8.92491 EndZ=0
    g16: ArcOfCircle CenterX=-5.7975 CenterY=10.8737 CenterZ=0 NormalX=0 NormalY=0 NormalZ=1 AngleXU=0 Radius=0.462832 StartAngle=0.759527 EndAngle=3.90112
    g17: ArcOfCircle CenterX=-3.64045 CenterY=8.60207 CenterZ=0 NormalX=0 NormalY=0 NormalZ=1 AngleXU=0 Radius=0.462832 StartAngle=3.90112 EndAngle=7.04271
    g18: LineSegment StartX=-6.13313 StartY=10.555 StartZ=0 EndX=-3.97607 EndY=8.28337 EndZ=0
    g19: LineSegment StartX=-5.46187 StartY=11.1924 StartZ=0 EndX=-3.30482 EndY=8.92076 EndZ=0
    g20: ArcOfCircle CenterX=-3.37745 CenterY=10.8693 CenterZ=0 NormalX=0 NormalY=0 NormalZ=1 AngleXU=0 Radius=0.462832 StartAngle=0.759527 EndAngle=3.90112
    g21: ArcOfCircle CenterX=-1.2204 CenterY=8.59765 CenterZ=0 NormalX=0 NormalY=0 NormalZ=1 AngleXU=0 Radius=0.462832 StartAngle=3.90112 EndAngle=7.04271
    g22: LineSegment StartX=-3.71308 StartY=10.5506 StartZ=0 EndX=-1.55603 EndY=8.27895 EndZ=0
    g23: LineSegment StartX=-3.04183 StartY=11.188 StartZ=0 EndX=-0.88477 EndY=8.91634 EndZ=0
    g24: ArcOfCircle CenterX=-0.748629 CenterY=10.8316 CenterZ=0 NormalX=0 NormalY=0 NormalZ=1 AngleXU=0 Radius=0.462832 StartAngle=0.759527 EndAngle=3.90112
    g25: ArcOfCircle CenterX=1.40843 CenterY=8.55994 CenterZ=0 NormalX=0 NormalY=0 NormalZ=1 AngleXU=0 Radius=0.462832 StartAngle=3.90112 EndAngle=7.04271
    g26: LineSegment StartX=-1.08426 StartY=10.5129 StartZ=0 EndX=1.0728 EndY=8.24124 EndZ=0
    g27: LineSegment StartX=-0.413001 StartY=11.1503 StartZ=0 EndX=1.74406 EndY=8.87863 EndZ=0
    g28: ArcOfCircle CenterX=1.67142 CenterY=10.8272 CenterZ=0 NormalX=0 NormalY=0 NormalZ=1 AngleXU=0 Radius=0.462832 StartAngle=0.759527 EndAngle=3.90112
    g29: ArcOfCircle CenterX=3.82848 CenterY=8.55552 CenterZ=0 NormalX=0 NormalY=0 NormalZ=1 AngleXU=0 Radius=0.462832 StartAngle=3.90112 EndAngle=7.04271
    g30: LineSegment StartX=1.33579 StartY=10.5085 StartZ=0 EndX=3.49285 EndY=8.23682 EndZ=0
    g31: LineSegment StartX=2.00705 StartY=11.1459 StartZ=0 EndX=4.1641 EndY=8.87421 EndZ=0
    g32: ArcOfCircle CenterX=4.35735 CenterY=10.823 CenterZ=0 NormalX=0 NormalY=0 NormalZ=1 AngleXU=0 Radius=0.462832 StartAngle=0.759527 EndAngle=3.90112
    g33: ArcOfCircle CenterX=6.51441 CenterY=8.55138 CenterZ=0 NormalX=0 NormalY=0 NormalZ=1 AngleXU=0 Radius=0.462832 StartAngle=3.90112 EndAngle=7.04271
    g34: LineSegment StartX=4.02172 StartY=10.5043 StartZ=0 EndX=6.17878 EndY=8.23268 EndZ=0
    g35: LineSegment StartX=4.69298 StartY=11.1417 StartZ=0 EndX=6.85003 EndY=8.87007 EndZ=0
    g36: ArcOfCircle CenterX=6.7774 CenterY=10.8186 CenterZ=0 NormalX=0 NormalY=0 NormalZ=1 AngleXU=0 Radius=0.462832 StartAngle=0.759527 EndAngle=3.90112
    g37: ArcOfCircle CenterX=8.93445 CenterY=8.54696 CenterZ=0 NormalX=0 NormalY=0 NormalZ=1 AngleXU=0 Radius=0.462832 StartAngle=3.90112 EndAngle=7.04271
    g38: LineSegment StartX=6.44177 StartY=10.4999 StartZ=0 EndX=8.59882 EndY=8.22826 EndZ=0
    g39: LineSegment StartX=7.11302 StartY=11.1373 StartZ=0 EndX=9.27008 EndY=8.86565 EndZ=0
    g40: ArcOfCircle CenterX=-9.27163 CenterY=5.08459 CenterZ=0 NormalX=0 NormalY=0 NormalZ=1 AngleXU=0 Radius=0.46354 StartAngle=0.744919 EndAngle=3.88651
    g41: ArcOfCircle CenterX=-7.12381 CenterY=2.75545 CenterZ=0 NormalX=0 NormalY=0 NormalZ=1 AngleXU=0 Radius=0.46354 StartAngle=3.88651 EndAngle=7.0281
    g42: LineSegment StartX=-9.6124 StartY=4.77035 StartZ=0 EndX=-7.46458 EndY=2.44121 EndZ=0
    g43: LineSegment StartX=-8.93086 StartY=5.39883 StartZ=0 EndX=-6.78304 EndY=3.06969 EndZ=0
    g44: ArcOfCircle CenterX=-6.83637 CenterY=5.15451 CenterZ=0 NormalX=0 NormalY=0 NormalZ=1 AngleXU=0 Radius=0.464019 StartAngle=0.744919 EndAngle=3.88651
    g45: ArcOfCircle CenterX=-4.59537 CenterY=2.72432 CenterZ=0 NormalX=0 NormalY=0 NormalZ=1 AngleXU=0 Radius=0.464019 StartAngle=3.88651 EndAngle=7.0281
    g46: LineSegment StartX=-7.17749 StartY=4.83995 StartZ=0 EndX=-4.93649 EndY=2.40976 EndZ=0
    g47: LineSegment StartX=-6.49525 StartY=5.46908 StartZ=0 EndX=-4.25425 EndY=3.03888 EndZ=0
    g48: ArcOfCircle CenterX=-4.29435 CenterY=5.09023 CenterZ=0 NormalX=0 NormalY=0 NormalZ=1 AngleXU=0 Radius=0.463144 StartAngle=0.744919 EndAngle=3.88651
    g49: ArcOfCircle CenterX=-2.04872 CenterY=2.65502 CenterZ=0 NormalX=0 NormalY=0 NormalZ=1 AngleXU=0 Radius=0.463144 StartAngle=3.88651 EndAngle=7.0281
    g50: LineSegment StartX=-3.95387 StartY=5.40421 StartZ=0 EndX=-1.70824 EndY=2.969 EndZ=0
    g51: LineSegment StartX=-4.63483 StartY=4.77626 StartZ=0 EndX=-2.3892 EndY=2.34105 EndZ=0
    g52: ArcOfCircle CenterX=-10.7939 CenterY=4.0488 CenterZ=0 NormalX=0 NormalY=0 NormalZ=1 AngleXU=0 Radius=0.47062 StartAngle=0.77714 EndAngle=3.91873
    g53: ArcOfCircle CenterX=-9.50133 CenterY=2.73468 CenterZ=0 NormalX=0 NormalY=0 NormalZ=1 AngleXU=0 Radius=0.47062 StartAngle=3.91873 EndAngle=7.06033
    g54: LineSegment StartX=-11.1294 StartY=3.71878 StartZ=0 EndX=-9.83685 EndY=2.40467 EndZ=0
    g55: LineSegment StartX=-10.4584 StartY=4.37882 StartZ=0 EndX=-9.16582 EndY=3.0647 EndZ=0
  constraints (74):
    c: Tangent(g0,g3) = 1.5708
    c: Tangent(g0,g2) = -1.5708
    c: Tangent(g2,g1) = -1.5708
    c: Tangent(g3,g1) = 1.5708
    c: Horizontal(g2)
    c: Equal(g0,g1)
    c: Tangent(g4,g7) = 1.5708
    c: Tangent(g4,g6) = -1.5708
    c: Tangent(g6,g5) = -1.5708
    c: Tangent(g7,g5) = 1.5708
    c: Horizontal(g6)
    c: Equal(g4,g5)
    c: Tangent(g8,g11) = 1.5708
    c: Tangent(g8,g10) = -1.5708
    c: Tangent(g10,g9) = -1.5708
    c: Tangent(g11,g9) = 1.5708
    c: Equal(g8,g9)
    c: Tangent(g12,g15) = 1.5708
    c: Tangent(g12,g14) = -1.5708
    c: Tangent(g14,g13) = -1.5708
    c: Tangent(g15,g13) = 1.5708
    c: Equal(g12,g13)
    c: Tangent(g16,g19) = 1.5708
    c: Tangent(g16,g18) = -1.5708
    c: Tangent(g18,g17) = -1.5708
    c: Tangent(g19,g17) = 1.5708
    c: Equal(g16,g17)
    c: Tangent(g20,g23) = 1.5708
    c: Tangent(g20,g22) = -1.5708
    c: Tangent(g22,g21) = -1.5708
    c: Tangent(g23,g21) = 1.5708
    c: Equal(g20,g21)
    c: Tangent(g24,g27) = 1.5708
    c: Tangent(g24,g26) = -1.5708
    c: Tangent(g26,g25) = -1.5708
    c: Tangent(g27,g25) = 1.5708
    c: Equal(g24,g25)
    c: Tangent(g28,g31) = 1.5708
    c: Tangent(g28,g30) = -1.5708
    c: Tangent(g30,g29) = -1.5708
    c: Tangent(g31,g29) = 1.5708
    c: Equal(g28,g29)
    c: Tangent(g32,g35) = 1.5708
    c: Tangent(g32,g34) = -1.5708
    c: Tangent(g34,g33) = -1.5708
    c: Tangent(g35,g33) = 1.5708
    c: Equal(g32,g33)
    c: Tangent(g36,g39) = 1.5708
    c: Tangent(g36,g38) = -1.5708
    c: Tangent(g38,g37) = -1.5708
    c: Tangent(g39,g37) = 1.5708
    c: Equal(g36,g37)
    c: Tangent(g40,g43) = 1.5708
    c: Tangent(g40,g42) = -1.5708
    c: Tangent(g42,g41) = -1.5708
    c: Tangent(g43,g41) = 1.5708
    c: Equal(g40,g41)
    c: Tangent(g44,g47) = 1.5708
    c: Tangent(g44,g46) = -1.5708
    c: Tangent(g46,g45) = -1.5708
    c: Tangent(g47,g45) = 1.5708
    c: Equal(g44,g45)
    c: Tangent(g48,g50) = 1.5708
    c: Tangent(g48,g51) = -1.5708
    c: Tangent(g51,g49) = -1.5708
    c: Tangent(g50,g49) = 1.5708
    c: Equal(g48,g49)
    c: Tangent(g52,g55) = 1.5708
    c: Tangent(g52,g54) = -1.5708
    c: Tangent(g54,g53) = -1.5708
    c: Tangent(g55,g53) = 1.5708
    c: Equal(g52,g53)
    c: Parallel(g43,g46)
    c: Parallel(g46,g51)
FEATURE [PartDesign::Pocket] Pocket006
  BaseFeature = -> Pocket005
  Length = 0.1
  Length2 = 100
  Profile = -> Sketch010
  Type = 0
FEATURE [Image::ImagePlane] ImagePlane004
  Placement = pos=(0,-1.5,9) rot=(0.591882,-0.54713,0.591882;4.14285rad)
  XSize = 55.91
  YSize = 36.36
FEATURE [Sketcher::SketchObject] Sketch011
  FullyConstrained = false
  MapMode = 5
  Placement = pos=(12.5133,0,0) rot=(0.57735,0.57735,0.57735;2.0944rad)
  Support = -> [Pocket006]
  sketch-geometry (73):
    g0: ArcOfCircle CenterX=-8.13859 CenterY=8.91768 CenterZ=0 NormalX=0 NormalY=0 NormalZ=1 AngleXU=0 Radius=0.348402 StartAngle=0.838326 EndAngle=3.97992
    g1: ArcOfCircle CenterX=-7.73682 CenterY=8.55634 CenterZ=0 NormalX=0 NormalY=0 NormalZ=1 AngleXU=0 Radius=0.348402 StartAngle=3.97992 EndAngle=7.12151
    g2: LineSegment StartX=-8.37157 StartY=8.65863 StartZ=0 EndX=-7.9698 EndY=8.2973 EndZ=0
    g3: LineSegment StartX=-7.90561 StartY=9.17673 StartZ=0 EndX=-7.50385 EndY=8.81539 EndZ=0
    g4: ArcOfCircle CenterX=-7.90609 CenterY=11.0862 CenterZ=0 NormalX=0 NormalY=0 NormalZ=1 AngleXU=0 Radius=0.468143 StartAngle=0.777539 EndAngle=3.91913
    g5: ArcOfCircle CenterX=-5.4971 CenterY=8.639 CenterZ=0 NormalX=0 NormalY=0 NormalZ=1 AngleXU=0 Radius=0.468143 StartAngle=3.91913 EndAngle=7.06072
    g6: LineSegment StartX=-8.23971 StartY=10.7577 StartZ=0 EndX=-5.83072 EndY=8.31059 EndZ=0
    g7: LineSegment StartX=-7.57248 StartY=11.4146 StartZ=0 EndX=-5.16349 EndY=8.96742 EndZ=0
    g8: ArcOfCircle CenterX=-5.68537 CenterY=11.251 CenterZ=0 NormalX=0 NormalY=0 NormalZ=1 AngleXU=0 Radius=0.466158 StartAngle=0.777539 EndAngle=3.91913
    g9: ArcOfCircle CenterX=-3.08113 CenterY=8.60552 CenterZ=0 NormalX=0 NormalY=0 NormalZ=1 AngleXU=0 Radius=0.466158 StartAngle=3.91913 EndAngle=7.06072
    g10: LineSegment StartX=-6.01757 StartY=10.924 StartZ=0 EndX=-3.41334 EndY=8.27849 EndZ=0
    g11: LineSegment StartX=-5.35317 StartY=11.578 StartZ=0 EndX=-2.74893 EndY=8.93254 EndZ=0
    g12: ArcOfCircle CenterX=-2.63925 CenterY=11.0704 CenterZ=0 NormalX=0 NormalY=0 NormalZ=1 AngleXU=0 Radius=0.490861 StartAngle=0.777539 EndAngle=3.91913
    g13: ArcOfCircle CenterX=-0.434424 CenterY=11.2971 CenterZ=0 NormalX=0 NormalY=0 NormalZ=1 AngleXU=0 Radius=0.466158 StartAngle=0.777539 EndAngle=3.91913
    g14: ArcOfCircle CenterX=-0.232371 CenterY=8.62544 CenterZ=0 NormalX=0 NormalY=0 NormalZ=1 AngleXU=0 Radius=0.490861 StartAngle=3.91913 EndAngle=7.06072
    g15: LineSegment StartX=-2.98906 StartY=10.7261 StartZ=0 EndX=-0.58218 EndY=8.28108 EndZ=0
    g16: LineSegment StartX=-2.28944 StartY=11.4148 StartZ=0 EndX=0.117437 EndY=8.96979 EndZ=0
    g17: ArcOfCircle CenterX=2.19955 CenterY=8.62138 CenterZ=0 NormalX=0 NormalY=0 NormalZ=1 AngleXU=0 Radius=0.466158 StartAngle=3.91913 EndAngle=7.06072
    g18: LineSegment StartX=-0.766627 StartY=10.9701 StartZ=0 EndX=1.86735 EndY=8.29436 EndZ=0
    g19: LineSegment StartX=-0.10222 StartY=11.6241 StartZ=0 EndX=2.53176 EndY=8.9484 EndZ=0
    g20: ArcOfCircle CenterX=2.19566 CenterY=11.0559 CenterZ=0 NormalX=0 NormalY=0 NormalZ=1 AngleXU=0 Radius=0.490861 StartAngle=0.777539 EndAngle=3.91913
    g21: ArcOfCircle CenterX=4.36987 CenterY=11.2873 CenterZ=0 NormalX=0 NormalY=0 NormalZ=1 AngleXU=0 Radius=0.466158 StartAngle=0.777539 EndAngle=3.91913
    g22: ArcOfCircle CenterX=4.60253 CenterY=8.61094 CenterZ=0 NormalX=0 NormalY=0 NormalZ=1 AngleXU=0 Radius=0.490861 StartAngle=3.91913 EndAngle=7.06072
    g23: LineSegment StartX=1.84586 StartY=10.7116 StartZ=0 EndX=4.25272 EndY=8.26659 EndZ=0
    g24: LineSegment StartX=2.54547 StartY=11.4003 StartZ=0 EndX=4.95234 EndY=8.95529 EndZ=0
    g25: ArcOfCircle CenterX=7.00446 CenterY=8.61094 CenterZ=0 NormalX=0 NormalY=0 NormalZ=1 AngleXU=0 Radius=0.466158 StartAngle=3.91913 EndAngle=7.06072
    g26: LineSegment StartX=4.03767 StartY=10.9602 StartZ=0 EndX=6.67226 EndY=8.28392 EndZ=0
    g27: LineSegment StartX=4.70208 StartY=11.6143 StartZ=0 EndX=7.33667 EndY=8.93796 EndZ=0
    g28: ArcOfCircle CenterX=6.763 CenterY=11.3915 CenterZ=0 NormalX=0 NormalY=0 NormalZ=1 AngleXU=0 Radius=0.466871 StartAngle=0.777539 EndAngle=3.91913
    g29: ArcOfCircle CenterX=9.3502 CenterY=8.76328 CenterZ=0 NormalX=0 NormalY=0 NormalZ=1 AngleXU=0 Radius=0.466871 StartAngle=3.91913 EndAngle=7.06072
    g30: LineSegment StartX=6.43029 StartY=11.0639 StartZ=0 EndX=9.01749 EndY=8.43575 EndZ=0
    g31: LineSegment StartX=7.09572 StartY=11.719 StartZ=0 EndX=9.68291 EndY=9.0908 EndZ=0
    g32: ArcOfCircle CenterX=-7.03074 CenterY=5.93733 CenterZ=0 NormalX=0 NormalY=0 NormalZ=1 AngleXU=0 Radius=0.468143 StartAngle=0.777539 EndAngle=3.91913
    g33: ArcOfCircle CenterX=-4.81002 CenterY=6.10219 CenterZ=0 NormalX=0 NormalY=0 NormalZ=1 AngleXU=0 Radius=0.466158 StartAngle=0.777539 EndAngle=3.91913
    g34: ArcOfCircle CenterX=-1.76389 CenterY=5.92162 CenterZ=0 NormalX=0 NormalY=0 NormalZ=1 AngleXU=0 Radius=0.490861 StartAngle=0.777539 EndAngle=3.91913
    g35: ArcOfCircle CenterX=0.440932 CenterY=6.14825 CenterZ=0 NormalX=0 NormalY=0 NormalZ=1 AngleXU=0 Radius=0.466158 StartAngle=0.777539 EndAngle=3.91913
    g36: ArcOfCircle CenterX=3.07102 CenterY=5.9071 CenterZ=0 NormalX=0 NormalY=0 NormalZ=1 AngleXU=0 Radius=0.490861 StartAngle=0.777539 EndAngle=3.91913
    g37: ArcOfCircle CenterX=5.24523 CenterY=6.13844 CenterZ=0 NormalX=0 NormalY=0 NormalZ=1 AngleXU=0 Radius=0.466158 StartAngle=0.777539 EndAngle=3.91913
    g38: ArcOfCircle CenterX=7.63836 CenterY=6.24263 CenterZ=0 NormalX=0 NormalY=0 NormalZ=1 AngleXU=0 Radius=0.466871 StartAngle=0.777539 EndAngle=3.91913
    g39: ArcOfCircle CenterX=-4.62175 CenterY=3.49018 CenterZ=0 NormalX=0 NormalY=0 NormalZ=1 AngleXU=0 Radius=0.468143 StartAngle=3.91913 EndAngle=7.06072
    g40: LineSegment StartX=-7.36436 StartY=5.60892 StartZ=0 EndX=-4.95537 EndY=3.16176 EndZ=0
    g41: LineSegment StartX=-6.69712 StartY=6.26575 StartZ=0 EndX=-4.28813 EndY=3.81859 EndZ=0
    g42: ArcOfCircle CenterX=-2.20578 CenterY=3.45669 CenterZ=0 NormalX=0 NormalY=0 NormalZ=1 AngleXU=0 Radius=0.466158 StartAngle=3.91913 EndAngle=7.06072
    g43: LineSegment StartX=-5.14222 StartY=5.77516 StartZ=0 EndX=-2.53798 EndY=3.12967 EndZ=0
    g44: LineSegment StartX=-4.47781 StartY=6.42921 StartZ=0 EndX=-1.87357 EndY=3.78371 EndZ=0
    g45: ArcOfCircle CenterX=0.642985 CenterY=3.47661 CenterZ=0 NormalX=0 NormalY=0 NormalZ=1 AngleXU=0 Radius=0.490861 StartAngle=3.91913 EndAngle=7.06072
    g46: LineSegment StartX=-2.1137 StartY=5.57727 StartZ=0 EndX=0.293176 EndY=3.13225 EndZ=0
    g47: LineSegment StartX=-1.41409 StartY=6.26597 StartZ=0 EndX=0.992793 EndY=3.82096 EndZ=0
    g48: ArcOfCircle CenterX=3.07491 CenterY=3.47255 CenterZ=0 NormalX=0 NormalY=0 NormalZ=1 AngleXU=0 Radius=0.466158 StartAngle=3.91913 EndAngle=7.06072
    g49: LineSegment StartX=0.108729 StartY=5.82123 StartZ=0 EndX=2.7427 EndY=3.14553 EndZ=0
    g50: LineSegment StartX=0.773136 StartY=6.47528 StartZ=0 EndX=3.40711 EndY=3.79957 EndZ=0
    g51: ArcOfCircle CenterX=5.47788 CenterY=3.46211 CenterZ=0 NormalX=0 NormalY=0 NormalZ=1 AngleXU=0 Radius=0.490861 StartAngle=3.91913 EndAngle=7.06072
    g52: LineSegment StartX=2.72121 StartY=5.56275 StartZ=0 EndX=5.12807 EndY=3.11776 EndZ=0
    g53: LineSegment StartX=3.42083 StartY=6.25146 StartZ=0 EndX=5.82769 EndY=3.80646 EndZ=0
    g54: ArcOfCircle CenterX=7.87982 CenterY=3.46211 CenterZ=0 NormalX=0 NormalY=0 NormalZ=1 AngleXU=0 Radius=0.466158 StartAngle=3.91913 EndAngle=7.06072
    g55: LineSegment StartX=4.91302 StartY=5.81142 StartZ=0 EndX=7.54762 EndY=3.13509 EndZ=0
    g56: LineSegment StartX=5.57743 StartY=6.46546 StartZ=0 EndX=8.21202 EndY=3.78913 EndZ=0
    g57: ArcOfCircle CenterX=10.2256 CenterY=3.61445 CenterZ=0 NormalX=0 NormalY=0 NormalZ=1 AngleXU=0 Radius=0.466871 StartAngle=3.91913 EndAngle=7.06072
    g58: LineSegment StartX=7.30565 StartY=5.91511 StartZ=0 EndX=9.89284 EndY=3.28692 EndZ=0
    g59: LineSegment StartX=7.97107 StartY=6.57016 StartZ=0 EndX=10.5583 EndY=3.94197 EndZ=0
    g60: ArcOfCircle CenterX=9.91477 CenterY=6.4674 CenterZ=0 NormalX=0 NormalY=0 NormalZ=1 AngleXU=0 Radius=0.509307 StartAngle=0.734657 EndAngle=3.87625
    g61: ArcOfCircle CenterX=10.5081 CenterY=5.81062 CenterZ=0 NormalX=0 NormalY=0 NormalZ=1 AngleXU=0 Radius=0.509307 StartAngle=3.87625 EndAngle=7.01784
    g62: LineSegment StartX=9.53683 StartY=6.126 StartZ=0 EndX=10.1301 EndY=5.46921 EndZ=0
    g63: LineSegment StartX=10.2927 StartY=6.80881 StartZ=0 EndX=10.886 EndY=6.15202 EndZ=0
    g64: ArcOfCircle CenterX=9.3711 CenterY=11.1921 CenterZ=0 NormalX=0 NormalY=0 NormalZ=1 AngleXU=0 Radius=0.474154 StartAngle=0.800404 EndAngle=3.942
    g65: ArcOfCircle CenterX=10.6298 CenterY=9.97065 CenterZ=0 NormalX=0 NormalY=0 NormalZ=1 AngleXU=0 Radius=0.474154 StartAngle=3.942 EndAngle=7.08359
    g66: LineSegment StartX=9.04089 StartY=10.8519 StartZ=0 EndX=10.2996 EndY=9.63038 EndZ=0
    g67: LineSegment StartX=9.7013 StartY=11.5324 StartZ=0 EndX=10.96 EndY=10.3109 EndZ=0
    g68: Circle CenterX=-7.17822 CenterY=3.25434 CenterZ=0 NormalX=0 NormalY=0 NormalZ=1 AngleXU=0 Radius=0.859538
    g69: Circle CenterX=-8.79322 CenterY=5.39085 CenterZ=0 NormalX=0 NormalY=0 NormalZ=1 AngleXU=0 Radius=0.809248
    g70: LineSegment StartX=-9.82381 StartY=3.80255 StartZ=0 EndX=-8.76206 EndY=3.193 EndZ=0
    g71: LineSegment StartX=-8.76206 StartY=3.193 StartZ=0 EndX=-9.82381 EndY=2.55595 EndZ=0
    g72: LineSegment StartX=-9.82381 StartY=2.55595 StartZ=0 EndX=-9.82381 EndY=3.80255 EndZ=0
  constraints (101):
    c: Tangent(g0,g3) = 1.5708
    c: Tangent(g0,g2) = -1.5708
    c: Tangent(g2,g1) = -1.5708
    c: Tangent(g3,g1) = 1.5708
    c: Equal(g0,g1)
    c: Tangent(g4,g7) = 1.5708
    c: Tangent(g4,g6) = -1.5708
    c: Tangent(g6,g5) = -1.5708
    c: Tangent(g7,g5) = 1.5708
    c: Equal(g4,g5)
    c: Tangent(g8,g11) = 1.5708
    c: Tangent(g8,g10) = -1.5708
    c: Tangent(g10,g9) = -1.5708
    c: Tangent(g11,g9) = 1.5708
    c: Equal(g8,g9)
    c: Tangent(g12,g16) = 1.5708
    c: Tangent(g12,g15) = -1.5708
    c: Tangent(g15,g14) = -1.5708
    c: Tangent(g16,g14) = 1.5708
    c: Equal(g12,g14)
    c: Tangent(g13,g19) = 1.5708
    c: Tangent(g13,g18) = -1.5708
    c: Tangent(g18,g17) = -1.5708
    c: Tangent(g19,g17) = 1.5708
    c: Equal(g13,g17)
    c: Tangent(g20,g24) = 1.5708
    c: Tangent(g20,g23) = -1.5708
    c: Tangent(g23,g22) = -1.5708
    c: Tangent(g24,g22) = 1.5708
    c: Equal(g20,g22)
    c: Tangent(g21,g27) = 1.5708
    c: Tangent(g21,g26) = -1.5708
    c: Tangent(g26,g25) = -1.5708
    c: Tangent(g27,g25) = 1.5708
    c: Equal(g21,g25)
    c: Tangent(g28,g31) = 1.5708
    c: Tangent(g28,g30) = -1.5708
    c: Tangent(g30,g29) = -1.5708
    c: Tangent(g31,g29) = 1.5708
    c: Equal(g28,g29)
    c: Parallel(g6,g10)
    c: Parallel(g10,g15)
    c: Parallel(g15,g18)
    c: Parallel(g18,g23)
    c: Parallel(g23,g26)
    c: Parallel(g26,g30)
    c: Tangent(g32,g41) = 1.5708
    c: Tangent(g32,g40) = -1.5708
    c: Tangent(g40,g39) = -1.5708
    c: Tangent(g41,g39) = 1.5708
    c: Equal(g32,g39)
    c: Tangent(g33,g44) = 1.5708
    c: Tangent(g33,g43) = -1.5708
    c: Tangent(g43,g42) = -1.5708
    c: Tangent(g44,g42) = 1.5708
    c: Equal(g33,g42)
    c: Tangent(g34,g47) = 1.5708
    c: Tangent(g34,g46) = -1.5708
    c: Tangent(g46,g45) = -1.5708
    c: Tangent(g47,g45) = 1.5708
    c: Equal(g34,g45)
    c: Tangent(g35,g50) = 1.5708
    c: Tangent(g35,g49) = -1.5708
    c: Tangent(g49,g48) = -1.5708
    c: Tangent(g50,g48) = 1.5708
    c: Equal(g35,g48)
    c: Tangent(g36,g53) = 1.5708
    c: Tangent(g36,g52) = -1.5708
    c: Tangent(g52,g51) = -1.5708
    c: Tangent(g53,g51) = 1.5708
    c: Equal(g36,g51)
    c: Tangent(g37,g56) = 1.5708
    c: Tangent(g37,g55) = -1.5708
    c: Tangent(g55,g54) = -1.5708
    c: Tangent(g56,g54) = 1.5708
    c: Equal(g37,g54)
    c: Tangent(g38,g59) = 1.5708
    c: Tangent(g38,g58) = -1.5708
    c: Tangent(g58,g57) = -1.5708
    c: Tangent(g59,g57) = 1.5708
    c: Equal(g38,g57)
    c: Parallel(g40,g43)
    c: Parallel(g43,g46)
    c: Parallel(g46,g49)
    c: Parallel(g49,g52)
    c: Parallel(g52,g55)
    c: Parallel(g55,g58)
    c: Tangent(g60,g63) = 1.5708
    c: Tangent(g60,g62) = -1.5708
    c: Tangent(g62,g61) = -1.5708
    c: Tangent(g63,g61) = 1.5708
    c: Equal(g60,g61)
    c: Tangent(g64,g67) = 1.5708
    c: Tangent(g64,g66) = -1.5708
    c: Tangent(g66,g65) = -1.5708
    c: Tangent(g67,g65) = 1.5708
    c: Equal(g64,g65)
    c: Coincident(g70,g71)
    c: Coincident(g71,g72)
    c: Coincident(g72,g70)
    c: Vertical(g72)
FEATURE [PartDesign::Pocket] Pocket007
  BaseFeature = -> Pocket006
  Length = 0.1
  Length2 = 100
  Profile = -> Sketch011
  Type = 0
FEATURE [PartDesign::Pocket] Pocket008
  BaseFeature = -> Pocket007
  Length = 10
  Length2 = 100
  Profile = -> Pocket007 [Face665]
  Type = 0
FEATURE [Sketcher::SketchObject] Sketch012
  FullyConstrained = false
  MapMode = 5
  Placement = pos=(0,-14.8386,6.1e-15) rot=(1,0,0;1.5708rad)
  Support = -> [Pocket008]
  sketch-geometry (4):
    g0: LineSegment StartX=-6.12442 StartY=3.67141 StartZ=0 EndX=0.619298 EndY=3.67141 EndZ=0
    g1: LineSegment StartX=0.619298 StartY=3.67141 StartZ=0 EndX=0.619298 EndY=1.28046 EndZ=0
    g2: LineSegment StartX=0.619298 StartY=1.28046 StartZ=0 EndX=-6.12442 EndY=1.28046 EndZ=0
    g3: LineSegment StartX=-6.12442 StartY=1.28046 StartZ=0 EndX=-6.12442 EndY=3.67141 EndZ=0
  constraints (8):
    c: Coincident(g0,g1)
    c: Coincident(g1,g2)
    c: Coincident(g2,g3)
    c: Coincident(g3,g0)
    c: Horizontal(g0)
    c: Horizontal(g2)
    c: Vertical(g1)
    c: Vertical(g3)
FEATURE [PartDesign::Pocket] Pocket009
  BaseFeature = -> Pocket008
  Length = 5
  Length2 = 100
  Profile = -> Sketch012
  Type = 0
FEATURE [PartDesign::Body] Body
  Group = -> [Sketch,Pad,Sketch001,Pocket,Sketch002,Pocket001,Sketch003,Groove,Sketch004,Sketch005,SubtractivePipe,Sketch006,Pocket002,Sketch007,Pocket003,Sketch008,Pocket004,Sketch009,Pocket005,Sketch010,Pocket006,Sketch011,Pocket007,Pocket008,Sketch012,Pocket009]
  Origin = -> Origin
  Tip = -> Pocket009
FEATURE [Mesh::Feature] Lumenier_QAV_S_Mini_DJI_O3_Antenna_Mount  label="Lumenier_QAV-S_Mini_DJI_O3_Antenna_Mount"
  Placement = pos=(0,0,20) rot=(0,0,1;0rad)
